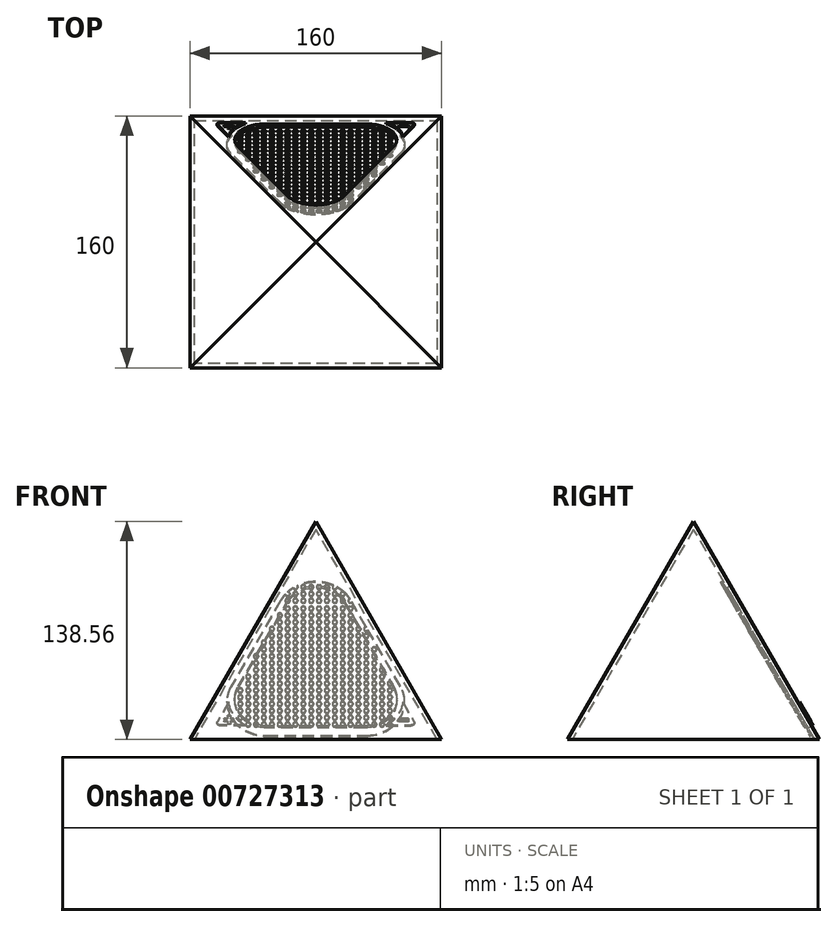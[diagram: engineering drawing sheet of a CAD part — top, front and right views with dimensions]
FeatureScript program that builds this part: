
annotation { "Feature Type Name" : "Feature", "Feature Type Description" : "" }
export const myFeature = defineFeature(function(context is Context, id is Id, definition is map)
    precondition{}
    {
        {
            var Q0;
            Q0=qCreatedBy(makeId("Top.planeOp"),FACE);
            var sketch = newSketch(context, id + "F0", { "sketchPlane" : qUnion([Q0])});
            skLineSegment(sketch, "E0.bottom", {"start": v(-50, 80) * mm, "end": v(50, 80) * mm});
            skLineSegment(sketch, "E0.top", {"start": v(-50, -80) * mm, "end": v(50, -80) * mm});
            skLineSegment(sketch, "E0.left", {"start": v(-80, 50) * mm, "end": v(-80, -50) * mm});
            skLineSegment(sketch, "E0.right", {"start": v(80, 50) * mm, "end": v(80, -50) * mm});
            skPoint(sketch, "E0.middle", {"position": v(0, 0) * mm});
            skLineSegment(sketch, "E1", {"start": v(-50, 80) * mm, "end": v(-50, -80) * mm, "construction": true});
            skLineSegment(sketch, "E2", {"start": v(50, 80) * mm, "end": v(50, -80) * mm, "construction": true});
            skLineSegment(sketch, "E3", {"start": v(80, 50) * mm, "end": v(-80, 50) * mm, "construction": true});
            skLineSegment(sketch, "E4", {"start": v(80, -50) * mm, "end": v(-80, -50) * mm, "construction": true});
            skPoint(sketch, "E5.orphan", {"position": v(-80, 80) * mm});
            skPoint(sketch, "E6.orphan", {"position": v(80, 80) * mm});
            skPoint(sketch, "E7.orphan", {"position": v(80, -80) * mm});
            skPoint(sketch, "E8.orphan", {"position": v(-80, -80) * mm});
            skLineSegment(sketch, "E9", {"start": v(-50, 80) * mm, "end": v(-80, 80) * mm});
            skLineSegment(sketch, "E10", {"start": v(-80, 80) * mm, "end": v(-80, 50) * mm});
            skLineSegment(sketch, "E11", {"start": v(80, 50) * mm, "end": v(80, 80) * mm});
            skLineSegment(sketch, "E12", {"start": v(80, 80) * mm, "end": v(50, 80) * mm});
            skLineSegment(sketch, "E13", {"start": v(80, -50) * mm, "end": v(80, -80) * mm});
            skLineSegment(sketch, "E14", {"start": v(80, -80) * mm, "end": v(50, -80) * mm});
            skLineSegment(sketch, "E15", {"start": v(-50, -80) * mm, "end": v(-80, -80) * mm});
            skLineSegment(sketch, "E16", {"start": v(-80, -80) * mm, "end": v(-80, -50) * mm});
            skSolve(sketch);
        }
        {
            var Q0;
            Q0=makeQuery(id+"F0.imprint","IMPRINT",FACE,{"disambiguationData":[TD([[makeQuery(id+"F0.imprint","IMPRINT",EDGE,{"derivedFrom":sQuery(id+"F0.wireOp",EDGE,"E0.bottom")}),-1.0]])]});
            extrude(context, id + "F1", {"entities" : qUnion([Q0]), "depth" : 139 * mm, "hasDraft" : true, "draftAngle" : 30 * degree, "draftPullDirection" : true});
        }
        {
            var Q0;
            Q0=makeQuery(id+"F1.opExtrude","CAP_FACE",FACE,{"disambiguationData":[OSD([sQuery(id+"F0.wireOp",EDGE,"E0.bottom"),sQuery(id+"F0.wireOp",EDGE,"E0.top"),sQuery(id+"F0.wireOp",EDGE,"E0.left"),sQuery(id+"F0.wireOp",EDGE,"E0.right"),sQuery(id+"F0.wireOp",EDGE,"E9"),sQuery(id+"F0.wireOp",EDGE,"E10"),sQuery(id+"F0.wireOp",EDGE,"E11"),sQuery(id+"F0.wireOp",EDGE,"E12"),sQuery(id+"F0.wireOp",EDGE,"E13"),sQuery(id+"F0.wireOp",EDGE,"E14"),sQuery(id+"F0.wireOp",EDGE,"E15"),sQuery(id+"F0.wireOp",EDGE,"E16")])],"isStart":true});
            shell(context, id + "F2", {"entities" : qUnion([Q0]), "thickness" : 2.5 * mm});
        }
        {
            var Q0;
            Q0=makeQuery(id+"F1.opExtrude","SWEPT_FACE",FACE,{"disambiguationData":[OSD([sQuery(id+"F0.wireOp",EDGE,"E0.bottom"),sQuery(id+"F0.wireOp",EDGE,"E9"),sQuery(id+"F0.wireOp",EDGE,"E12")])]});
            var sketch = newSketch(context, id + "F3", { "sketchPlane" : qUnion([Q0])});
            skCircle(sketch, "E17", {"center": v(0, 20) * mm, "radius": 33 * mm});
            skSolve(sketch);
        }
        {
            var Q0;
            Q0=makeQuery(id+"F3.imprint","IMPRINT",FACE,{"disambiguationData":[TD([[makeQuery(id+"F3.imprint","IMPRINT",EDGE,{"derivedFrom":sQuery(id+"F3.wireOp",EDGE,"E17")}),-1.0]])]});
            var sketch = newSketch(context, id + "F4", { "sketchPlane" : qUnion([Q0])});
            skCircle(sketch, "E18.0", {"center": v(0, 20) * mm, "radius": 33 * mm, "construction": true});
            skLineSegment(sketch, "E19.0", {"start": v(-31.46, -30) * mm, "end": v(31.46, -30) * mm});
            skLineSegment(sketch, "E19.1", {"start": v(-17.89, 61.86) * mm, "end": v(-49.35, -1.06) * mm});
            skLineSegment(sketch, "E19.2", {"start": v(49.35, -1.06) * mm, "end": v(17.89, 61.86) * mm});
            skPoint(sketch, "E20.visualSharp", {"position": v(0, 97.64) * mm});
            skArc(sketch, "E20.filletArc", {"start": v(17.89, 61.86) * mm, "mid": v(0, 72.92) * mm, "end": v(-17.89, 61.86) * mm});
            skPoint(sketch, "E21.visualSharp", {"position": v(63.82, -30) * mm});
            skArc(sketch, "E21.filletArc", {"start": v(31.46, -30) * mm, "mid": v(48.47, -20.51) * mm, "end": v(49.35, -1.06) * mm});
            skPoint(sketch, "E22.visualSharp", {"position": v(-63.82, -30) * mm});
            skArc(sketch, "E22.filletArc", {"start": v(-49.35, -1.06) * mm, "mid": v(-48.47, -20.51) * mm, "end": v(-31.46, -30) * mm});
            skSolve(sketch);
        }
        {
            var Q0;
            Q0=qSketchRegion(id+"F4",true);
            extrude(context, id + "F5", {"entities" : qUnion([Q0]), "operationType" : NewBodyOperationType.REMOVE, "oppositeDirection" : true, "depth" : 25 * mm, "offsetDistance" : 25 * mm});
        }
        {
            var Q0;
            Q0=makeQuery(id+"F3.imprint","IMPRINT",FACE,{"disambiguationData":[TD([[makeQuery(id+"F3.imprint","IMPRINT",EDGE,{"derivedFrom":sQuery(id+"F3.wireOp",EDGE,"E17")}),-1.0]])]});
            var sketch = newSketch(context, id + "F6", { "sketchPlane" : qUnion([Q0])});
            skArc(sketch, "E23.2", {"start": v(-55.28, -12.92) * mm, "mid": v(-51.87, -22.62) * mm, "end": v(-44.73, -30) * mm});
            skLineSegment(sketch, "E24", {"start": v(-44.73, -30) * mm, "end": v(-60.58, -30) * mm});
            skPoint(sketch, "E24.startSnap0", {"position": v(0, -34) * mm});
            skPoint(sketch, "E25.visualSharp", {"position": v(-63.82, -30) * mm});
            skArc(sketch, "E25.filletArc", {"start": v(-62.37, -27.1) * mm, "mid": v(-62.28, -29.05) * mm, "end": v(-60.58, -30) * mm});
            skPoint(sketch, "E26.orphan", {"position": v(-31.46, -34) * mm});
            skPoint(sketch, "E27.orphan", {"position": v(0, -30) * mm});
            skLineSegment(sketch, "E28.trimOffspring", {"start": v(-55.28, -12.92) * mm, "end": v(-62.37, -27.1) * mm});
            skPoint(sketch, "E29.0.start.orphan", {"position": v(-17.89, 61.86) * mm});
            skPoint(sketch, "E30.end.orphan", {"position": v(-49.35, -1.06) * mm});
            skPoint(sketch, "E23.0.start.orphan", {"position": v(31.46, -34) * mm});
            skPoint(sketch, "E31.0", {"position": v(0, 0) * mm});
            skLineSegment(sketch, "E32", {"start": v(0, 0) * mm, "end": v(0, 39.55) * mm, "construction": true});
            skLineSegment(sketch, "E33.MirrorCS", {"start": v(55.28, -12.92) * mm, "end": v(62.37, -27.1) * mm});
            skArc(sketch, "E34.MirrorCS", {"start": v(55.28, -12.92) * mm, "mid": v(51.87, -22.62) * mm, "end": v(44.73, -30) * mm});
            skLineSegment(sketch, "E35.MirrorCS", {"start": v(44.73, -30) * mm, "end": v(60.58, -30) * mm});
            skArc(sketch, "E36.MirrorCS", {"start": v(62.37, -27.1) * mm, "mid": v(62.28, -29.05) * mm, "end": v(60.58, -30) * mm});
            skSolve(sketch);
        }
        {
            var Q0;
            Q0=makeQuery(id+"F6.imprint","IMPRINT",FACE,{"disambiguationData":[TD([[makeQuery(id+"F6.imprint","IMPRINT",EDGE,{"derivedFrom":sQuery(id+"F6.wireOp",EDGE,"E23.2")}),-1.0]])]});
            var Q1;
            Q1=makeQuery(id+"F6.imprint","IMPRINT",FACE,{"disambiguationData":[TD([[makeQuery(id+"F6.imprint","IMPRINT",EDGE,{"derivedFrom":sQuery(id+"F6.wireOp",EDGE,"E33.MirrorCS")}),-1.0]])]});
            extrude(context, id + "F7", {"entities" : qUnion([Q0, Q1]), "operationType" : NewBodyOperationType.ADD, "depth" : 1 * mm, "offsetDistance" : 25 * mm});
        }
        {
            var Q0;
            Q0=makeQuery(id+"F7.opExtrude","CAP_FACE",FACE,{"disambiguationData":[OSD([sQuery(id+"F6.wireOp",EDGE,"E23.2"),sQuery(id+"F6.wireOp",EDGE,"E24"),sQuery(id+"F6.wireOp",EDGE,"E25.filletArc"),sQuery(id+"F6.wireOp",EDGE,"E28.trimOffspring")])],"isStart":false});
            var sketch = newSketch(context, id + "F8", { "sketchPlane" : qUnion([Q0])});
            skLineSegment(sketch, "E37.bottom", {"start": v(-58.9, -25) * mm, "end": v(-52.9, -25) * mm});
            skLineSegment(sketch, "E37.top", {"start": v(-58.9, -27) * mm, "end": v(-52.9, -27) * mm});
            skLineSegment(sketch, "E37.left", {"start": v(-58.9, -25) * mm, "end": v(-58.9, -27) * mm});
            skLineSegment(sketch, "E37.right", {"start": v(-52.9, -25) * mm, "end": v(-52.9, -27) * mm});
            skLineSegment(sketch, "E38.bottom", {"start": v(52.13, -25) * mm, "end": v(54.13, -25) * mm});
            skLineSegment(sketch, "E38.top", {"start": v(52.13, -27) * mm, "end": v(54.13, -27) * mm});
            skLineSegment(sketch, "E38.left", {"start": v(52.13, -25) * mm, "end": v(52.13, -27) * mm});
            skLineSegment(sketch, "E38.right", {"start": v(58.13, -25) * mm, "end": v(58.13, -27) * mm});
            skLineSegment(sketch, "E39.bottom", {"start": v(54.13, -23) * mm, "end": v(56.13, -23) * mm});
            skLineSegment(sketch, "E39.top", {"start": v(54.13, -29) * mm, "end": v(56.13, -29) * mm});
            skLineSegment(sketch, "E39.left", {"start": v(54.13, -23) * mm, "end": v(54.13, -25) * mm});
            skLineSegment(sketch, "E39.right", {"start": v(56.13, -23) * mm, "end": v(56.13, -25) * mm});
            skPoint(sketch, "E39.middle", {"position": v(55.13, -26) * mm});
            skPoint(sketch, "E39.middle.positionSnap0", {"position": v(55.13, -27) * mm});
            skPoint(sketch, "E39.centerSnap0", {"position": v(55.13, -27) * mm});
            skLineSegment(sketch, "E40.trimOffspring", {"start": v(54.13, -27) * mm, "end": v(54.13, -29) * mm});
            skLineSegment(sketch, "E41.trimOffspring", {"start": v(56.13, -25) * mm, "end": v(58.13, -25) * mm});
            skLineSegment(sketch, "E42.trimOffspring", {"start": v(56.13, -27) * mm, "end": v(56.13, -29) * mm});
            skLineSegment(sketch, "E43.trimOffspring", {"start": v(56.13, -27) * mm, "end": v(58.13, -27) * mm});
            skSolve(sketch);
        }
        {
            var Q0;
            Q0=makeQuery(id+"F8.imprint","IMPRINT",FACE,{"disambiguationData":[TD([[makeQuery(id+"F8.imprint","IMPRINT",EDGE,{"derivedFrom":sQuery(id+"F8.wireOp",EDGE,"E37.bottom")}),-1.0]])]});
            var Q1;
            Q1=makeQuery(id+"F8.imprint","IMPRINT",FACE,{"disambiguationData":[TD([[makeQuery(id+"F8.imprint","IMPRINT",EDGE,{"derivedFrom":sQuery(id+"F8.wireOp",EDGE,"E38.bottom")}),-1.0]])]});
            extrude(context, id + "F9", {"entities" : qUnion([Q0, Q1]), "operationType" : NewBodyOperationType.REMOVE, "oppositeDirection" : true, "depth" : 1 * mm, "offsetDistance" : 25 * mm});
        }
        {
            var Q0;
            Q0=qCreatedBy(makeId("Right.planeOp"),FACE);
            var sketch = newSketch(context, id + "F10", { "sketchPlane" : qUnion([Q0])});
            skPoint(sketch, "E44.0", {"position": v(73.92, 8.04) * mm});
            skCircle(sketch, "E45", {"center": v(73.92, 8.04) * mm, "radius": 1.5 * mm});
            skSolve(sketch);
        }
        {
            var Q0;
            Q0=makeQuery(id+"F2.opShell","OFFSET_FACE",FACE,{"disambiguationData":[OSD([sQuery(id+"F0.wireOp",EDGE,"E0.bottom"),sQuery(id+"F0.wireOp",EDGE,"E9"),sQuery(id+"F0.wireOp",EDGE,"E12")])]});
            cPlane(context, id + "F11", {"entities" : qUnion([Q0]), "cplaneType" : CPlaneType.OFFSET, "offset" : 1 * mm, "width" : 150 * mm, "height" : 150 * mm});
        }
        {
            var Q0;
            Q0=qCreatedBy(id+"F11.planeOp",FACE);
            var sketch = newSketch(context, id + "F12", { "sketchPlane" : qUnion([Q0])});
            skArc(sketch, "E46.0", {"start": v(22.36, 64.1) * mm, "mid": v(0, 77.92) * mm, "end": v(-22.36, 64.1) * mm});
            skArc(sketch, "E46.1", {"start": v(-53.82, 1.18) * mm, "mid": v(-52.73, -23.14) * mm, "end": v(-31.46, -35) * mm});
            skLineSegment(sketch, "E46.2", {"start": v(-31.46, -35) * mm, "end": v(31.46, -35) * mm});
            skLineSegment(sketch, "E46.3", {"start": v(-22.36, 64.1) * mm, "end": v(-53.82, 1.18) * mm});
            skArc(sketch, "E46.4", {"start": v(31.46, -35) * mm, "mid": v(52.73, -23.14) * mm, "end": v(53.82, 1.18) * mm});
            skLineSegment(sketch, "E46.5", {"start": v(53.82, 1.18) * mm, "end": v(22.36, 64.1) * mm});
            skSolve(sketch);
        }
        {
            var Q0;
            Q0=qSketchRegion(id+"F12",true);
            extrude(context, id + "F13", {"entities" : qUnion([Q0]), "depth" : 1 * mm, "offsetDistance" : 25 * mm});
        }
        {
            var Q0;
            Q0=makeQuery(id+"F13.opExtrude","CAP_FACE",FACE,{"disambiguationData":[OSD([sQuery(id+"F12.wireOp",EDGE,"E46.0"),sQuery(id+"F12.wireOp",EDGE,"E46.1"),sQuery(id+"F12.wireOp",EDGE,"E46.2"),sQuery(id+"F12.wireOp",EDGE,"E46.3"),sQuery(id+"F12.wireOp",EDGE,"E46.4"),sQuery(id+"F12.wireOp",EDGE,"E46.5")])],"isStart":false});
            var sketch = newSketch(context, id + "F14", { "sketchPlane" : qUnion([Q0])});
            skCircle(sketch, "E47.0.1.2", {"center": v(-22.93, -26.66) * mm, "radius": 1.5 * mm});
            skCircle(sketch, "E47.0.1.4", {"center": v(-7.93, -26.66) * mm, "radius": 1.5 * mm});
            skCircle(sketch, "E47.0.1.5", {"center": v(-12.93, -26.66) * mm, "radius": 1.5 * mm});
            skCircle(sketch, "E47.0.1.6", {"center": v(-37.93, -26.66) * mm, "radius": 1.5 * mm});
            skCircle(sketch, "E47.0.1.9", {"center": v(42.07, -26.66) * mm, "radius": 1.5 * mm});
            skCircle(sketch, "E47.0.1.10", {"center": v(27.07, -26.66) * mm, "radius": 1.5 * mm});
            skCircle(sketch, "E47.0.1.11", {"center": v(17.07, -26.66) * mm, "radius": 1.5 * mm});
            skCircle(sketch, "E47.0.1.12", {"center": v(2.07, -26.66) * mm, "radius": 1.5 * mm});
            skCircle(sketch, "E47.0.1.14", {"center": v(-32.93, -26.66) * mm, "radius": 1.5 * mm});
            skCircle(sketch, "E47.0.1.15", {"center": v(-17.93, -26.66) * mm, "radius": 1.5 * mm});
            skCircle(sketch, "E47.0.1.16", {"center": v(-27.93, -26.66) * mm, "radius": 1.5 * mm});
            skCircle(sketch, "E47.0.1.17", {"center": v(47.07, -26.66) * mm, "radius": 1.5 * mm});
            skCircle(sketch, "E47.0.1.18", {"center": v(37.07, -26.66) * mm, "radius": 1.5 * mm});
            skCircle(sketch, "E47.0.1.19", {"center": v(32.07, -26.66) * mm, "radius": 1.5 * mm});
            skCircle(sketch, "E47.0.1.20", {"center": v(22.07, -26.66) * mm, "radius": 1.5 * mm});
            skCircle(sketch, "E47.0.1.21", {"center": v(12.07, -26.66) * mm, "radius": 1.5 * mm});
            skCircle(sketch, "E47.0.1.22", {"center": v(7.07, -26.66) * mm, "radius": 1.5 * mm});
            skCircle(sketch, "E47.0.1.23", {"center": v(-2.93, -26.66) * mm, "radius": 1.5 * mm});
            skCircle(sketch, "E47.0.1.25", {"center": v(-42.93, -26.66) * mm, "radius": 1.5 * mm});
            skCircle(sketch, "E47.0.2.2", {"center": v(-22.93, -21.66) * mm, "radius": 1.5 * mm});
            skCircle(sketch, "E47.0.2.3", {"center": v(-47.93, -21.66) * mm, "radius": 1.5 * mm});
            skCircle(sketch, "E47.0.2.4", {"center": v(-7.93, -21.66) * mm, "radius": 1.5 * mm});
            skCircle(sketch, "E47.0.2.5", {"center": v(-12.93, -21.66) * mm, "radius": 1.5 * mm});
            skCircle(sketch, "E47.0.2.6", {"center": v(-37.93, -21.66) * mm, "radius": 1.5 * mm});
            skCircle(sketch, "E47.0.2.9", {"center": v(42.07, -21.66) * mm, "radius": 1.5 * mm});
            skCircle(sketch, "E47.0.2.10", {"center": v(27.07, -21.66) * mm, "radius": 1.5 * mm});
            skCircle(sketch, "E47.0.2.11", {"center": v(17.07, -21.66) * mm, "radius": 1.5 * mm});
            skCircle(sketch, "E47.0.2.12", {"center": v(2.07, -21.66) * mm, "radius": 1.5 * mm});
            skCircle(sketch, "E47.0.2.14", {"center": v(-32.93, -21.66) * mm, "radius": 1.5 * mm});
            skCircle(sketch, "E47.0.2.15", {"center": v(-17.93, -21.66) * mm, "radius": 1.5 * mm});
            skCircle(sketch, "E47.0.2.16", {"center": v(-27.93, -21.66) * mm, "radius": 1.5 * mm});
            skCircle(sketch, "E47.0.2.17", {"center": v(47.07, -21.66) * mm, "radius": 1.5 * mm});
            skCircle(sketch, "E47.0.2.18", {"center": v(37.07, -21.66) * mm, "radius": 1.5 * mm});
            skCircle(sketch, "E47.0.2.19", {"center": v(32.07, -21.66) * mm, "radius": 1.5 * mm});
            skCircle(sketch, "E47.0.2.20", {"center": v(22.07, -21.66) * mm, "radius": 1.5 * mm});
            skCircle(sketch, "E47.0.2.21", {"center": v(12.07, -21.66) * mm, "radius": 1.5 * mm});
            skCircle(sketch, "E47.0.2.22", {"center": v(7.07, -21.66) * mm, "radius": 1.5 * mm});
            skCircle(sketch, "E47.0.2.23", {"center": v(-2.93, -21.66) * mm, "radius": 1.5 * mm});
            skCircle(sketch, "E47.0.2.25", {"center": v(-42.93, -21.66) * mm, "radius": 1.5 * mm});
            skCircle(sketch, "E47.0.3.2", {"center": v(-22.93, -16.66) * mm, "radius": 1.5 * mm});
            skCircle(sketch, "E47.0.3.3", {"center": v(-47.93, -16.66) * mm, "radius": 1.5 * mm});
            skCircle(sketch, "E47.0.3.4", {"center": v(-7.93, -16.66) * mm, "radius": 1.5 * mm});
            skCircle(sketch, "E47.0.3.5", {"center": v(-12.93, -16.66) * mm, "radius": 1.5 * mm});
            skCircle(sketch, "E47.0.3.6", {"center": v(-37.93, -16.66) * mm, "radius": 1.5 * mm});
            skCircle(sketch, "E47.0.3.9", {"center": v(42.07, -16.66) * mm, "radius": 1.5 * mm});
            skCircle(sketch, "E47.0.3.10", {"center": v(27.07, -16.66) * mm, "radius": 1.5 * mm});
            skCircle(sketch, "E47.0.3.11", {"center": v(17.07, -16.66) * mm, "radius": 1.5 * mm});
            skCircle(sketch, "E47.0.3.12", {"center": v(2.07, -16.66) * mm, "radius": 1.5 * mm});
            skCircle(sketch, "E47.0.3.14", {"center": v(-32.93, -16.66) * mm, "radius": 1.5 * mm});
            skCircle(sketch, "E47.0.3.15", {"center": v(-17.93, -16.66) * mm, "radius": 1.5 * mm});
            skCircle(sketch, "E47.0.3.16", {"center": v(-27.93, -16.66) * mm, "radius": 1.5 * mm});
            skCircle(sketch, "E47.0.3.17", {"center": v(47.07, -16.66) * mm, "radius": 1.5 * mm});
            skCircle(sketch, "E47.0.3.18", {"center": v(37.07, -16.66) * mm, "radius": 1.5 * mm});
            skCircle(sketch, "E47.0.3.19", {"center": v(32.07, -16.66) * mm, "radius": 1.5 * mm});
            skCircle(sketch, "E47.0.3.20", {"center": v(22.07, -16.66) * mm, "radius": 1.5 * mm});
            skCircle(sketch, "E47.0.3.21", {"center": v(12.07, -16.66) * mm, "radius": 1.5 * mm});
            skCircle(sketch, "E47.0.3.22", {"center": v(7.07, -16.66) * mm, "radius": 1.5 * mm});
            skCircle(sketch, "E47.0.3.23", {"center": v(-2.93, -16.66) * mm, "radius": 1.5 * mm});
            skCircle(sketch, "E47.0.3.25", {"center": v(-42.93, -16.66) * mm, "radius": 1.5 * mm});
            skCircle(sketch, "E47.0.4.2", {"center": v(-22.93, -11.66) * mm, "radius": 1.5 * mm});
            skCircle(sketch, "E47.0.4.3", {"center": v(-47.93, -11.66) * mm, "radius": 1.5 * mm});
            skCircle(sketch, "E47.0.4.4", {"center": v(-7.93, -11.66) * mm, "radius": 1.5 * mm});
            skCircle(sketch, "E47.0.4.5", {"center": v(-12.93, -11.66) * mm, "radius": 1.5 * mm});
            skCircle(sketch, "E47.0.4.6", {"center": v(-37.93, -11.66) * mm, "radius": 1.5 * mm});
            skCircle(sketch, "E47.0.4.9", {"center": v(42.07, -11.66) * mm, "radius": 1.5 * mm});
            skCircle(sketch, "E47.0.4.10", {"center": v(27.07, -11.66) * mm, "radius": 1.5 * mm});
            skCircle(sketch, "E47.0.4.11", {"center": v(17.07, -11.66) * mm, "radius": 1.5 * mm});
            skCircle(sketch, "E47.0.4.12", {"center": v(2.07, -11.66) * mm, "radius": 1.5 * mm});
            skCircle(sketch, "E47.0.4.14", {"center": v(-32.93, -11.66) * mm, "radius": 1.5 * mm});
            skCircle(sketch, "E47.0.4.15", {"center": v(-17.93, -11.66) * mm, "radius": 1.5 * mm});
            skCircle(sketch, "E47.0.4.16", {"center": v(-27.93, -11.66) * mm, "radius": 1.5 * mm});
            skCircle(sketch, "E47.0.4.17", {"center": v(47.07, -11.66) * mm, "radius": 1.5 * mm});
            skCircle(sketch, "E47.0.4.18", {"center": v(37.07, -11.66) * mm, "radius": 1.5 * mm});
            skCircle(sketch, "E47.0.4.19", {"center": v(32.07, -11.66) * mm, "radius": 1.5 * mm});
            skCircle(sketch, "E47.0.4.20", {"center": v(22.07, -11.66) * mm, "radius": 1.5 * mm});
            skCircle(sketch, "E47.0.4.21", {"center": v(12.07, -11.66) * mm, "radius": 1.5 * mm});
            skCircle(sketch, "E47.0.4.22", {"center": v(7.07, -11.66) * mm, "radius": 1.5 * mm});
            skCircle(sketch, "E47.0.4.23", {"center": v(-2.93, -11.66) * mm, "radius": 1.5 * mm});
            skCircle(sketch, "E47.0.4.25", {"center": v(-42.93, -11.66) * mm, "radius": 1.5 * mm});
            skCircle(sketch, "E47.0.5.2", {"center": v(-22.93, -6.66) * mm, "radius": 1.5 * mm});
            skCircle(sketch, "E47.0.5.3", {"center": v(-47.93, -6.66) * mm, "radius": 1.5 * mm});
            skCircle(sketch, "E47.0.5.4", {"center": v(-7.93, -6.66) * mm, "radius": 1.5 * mm});
            skCircle(sketch, "E47.0.5.5", {"center": v(-12.93, -6.66) * mm, "radius": 1.5 * mm});
            skCircle(sketch, "E47.0.5.6", {"center": v(-37.93, -6.66) * mm, "radius": 1.5 * mm});
            skCircle(sketch, "E47.0.5.9", {"center": v(42.07, -6.66) * mm, "radius": 1.5 * mm});
            skCircle(sketch, "E47.0.5.10", {"center": v(27.07, -6.66) * mm, "radius": 1.5 * mm});
            skCircle(sketch, "E47.0.5.11", {"center": v(17.07, -6.66) * mm, "radius": 1.5 * mm});
            skCircle(sketch, "E47.0.5.12", {"center": v(2.07, -6.66) * mm, "radius": 1.5 * mm});
            skCircle(sketch, "E47.0.5.14", {"center": v(-32.93, -6.66) * mm, "radius": 1.5 * mm});
            skCircle(sketch, "E47.0.5.15", {"center": v(-17.93, -6.66) * mm, "radius": 1.5 * mm});
            skCircle(sketch, "E47.0.5.16", {"center": v(-27.93, -6.66) * mm, "radius": 1.5 * mm});
            skCircle(sketch, "E47.0.5.17", {"center": v(47.07, -6.66) * mm, "radius": 1.5 * mm});
            skCircle(sketch, "E47.0.5.18", {"center": v(37.07, -6.66) * mm, "radius": 1.5 * mm});
            skCircle(sketch, "E47.0.5.19", {"center": v(32.07, -6.66) * mm, "radius": 1.5 * mm});
            skCircle(sketch, "E47.0.5.20", {"center": v(22.07, -6.66) * mm, "radius": 1.5 * mm});
            skCircle(sketch, "E47.0.5.21", {"center": v(12.07, -6.66) * mm, "radius": 1.5 * mm});
            skCircle(sketch, "E47.0.5.22", {"center": v(7.07, -6.66) * mm, "radius": 1.5 * mm});
            skCircle(sketch, "E47.0.5.23", {"center": v(-2.93, -6.66) * mm, "radius": 1.5 * mm});
            skCircle(sketch, "E47.0.5.25", {"center": v(-42.93, -6.66) * mm, "radius": 1.5 * mm});
            skCircle(sketch, "E47.0.6.2", {"center": v(-22.93, -1.66) * mm, "radius": 1.5 * mm});
            skCircle(sketch, "E47.0.6.3", {"center": v(-47.93, -1.66) * mm, "radius": 1.5 * mm});
            skCircle(sketch, "E47.0.6.4", {"center": v(-7.93, -1.66) * mm, "radius": 1.5 * mm});
            skCircle(sketch, "E47.0.6.5", {"center": v(-12.93, -1.66) * mm, "radius": 1.5 * mm});
            skCircle(sketch, "E47.0.6.6", {"center": v(-37.93, -1.66) * mm, "radius": 1.5 * mm});
            skCircle(sketch, "E47.0.6.9", {"center": v(42.07, -1.66) * mm, "radius": 1.5 * mm});
            skCircle(sketch, "E47.0.6.10", {"center": v(27.07, -1.66) * mm, "radius": 1.5 * mm});
            skCircle(sketch, "E47.0.6.11", {"center": v(17.07, -1.66) * mm, "radius": 1.5 * mm});
            skCircle(sketch, "E47.0.6.12", {"center": v(2.07, -1.66) * mm, "radius": 1.5 * mm});
            skCircle(sketch, "E47.0.6.14", {"center": v(-32.93, -1.66) * mm, "radius": 1.5 * mm});
            skCircle(sketch, "E47.0.6.15", {"center": v(-17.93, -1.66) * mm, "radius": 1.5 * mm});
            skCircle(sketch, "E47.0.6.16", {"center": v(-27.93, -1.66) * mm, "radius": 1.5 * mm});
            skCircle(sketch, "E47.0.6.17", {"center": v(47.07, -1.66) * mm, "radius": 1.5 * mm});
            skCircle(sketch, "E47.0.6.18", {"center": v(37.07, -1.66) * mm, "radius": 1.5 * mm});
            skCircle(sketch, "E47.0.6.19", {"center": v(32.07, -1.66) * mm, "radius": 1.5 * mm});
            skCircle(sketch, "E47.0.6.20", {"center": v(22.07, -1.66) * mm, "radius": 1.5 * mm});
            skCircle(sketch, "E47.0.6.21", {"center": v(12.07, -1.66) * mm, "radius": 1.5 * mm});
            skCircle(sketch, "E47.0.6.22", {"center": v(7.07, -1.66) * mm, "radius": 1.5 * mm});
            skCircle(sketch, "E47.0.6.23", {"center": v(-2.93, -1.66) * mm, "radius": 1.5 * mm});
            skCircle(sketch, "E47.0.6.25", {"center": v(-42.93, -1.66) * mm, "radius": 1.5 * mm});
            skCircle(sketch, "E47.0.7.2", {"center": v(-22.93, 3.34) * mm, "radius": 1.5 * mm});
            skCircle(sketch, "E47.0.7.4", {"center": v(-7.93, 3.34) * mm, "radius": 1.5 * mm});
            skCircle(sketch, "E47.0.7.5", {"center": v(-12.93, 3.34) * mm, "radius": 1.5 * mm});
            skCircle(sketch, "E47.0.7.6", {"center": v(-37.93, 3.34) * mm, "radius": 1.5 * mm});
            skCircle(sketch, "E47.0.7.9", {"center": v(42.07, 3.34) * mm, "radius": 1.5 * mm});
            skCircle(sketch, "E47.0.7.10", {"center": v(27.07, 3.34) * mm, "radius": 1.5 * mm});
            skCircle(sketch, "E47.0.7.11", {"center": v(17.07, 3.34) * mm, "radius": 1.5 * mm});
            skCircle(sketch, "E47.0.7.12", {"center": v(2.07, 3.34) * mm, "radius": 1.5 * mm});
            skCircle(sketch, "E47.0.7.14", {"center": v(-32.93, 3.34) * mm, "radius": 1.5 * mm});
            skCircle(sketch, "E47.0.7.15", {"center": v(-17.93, 3.34) * mm, "radius": 1.5 * mm});
            skCircle(sketch, "E47.0.7.16", {"center": v(-27.93, 3.34) * mm, "radius": 1.5 * mm});
            skCircle(sketch, "E47.0.7.17", {"center": v(47.07, 3.34) * mm, "radius": 1.5 * mm});
            skCircle(sketch, "E47.0.7.18", {"center": v(37.07, 3.34) * mm, "radius": 1.5 * mm});
            skCircle(sketch, "E47.0.7.19", {"center": v(32.07, 3.34) * mm, "radius": 1.5 * mm});
            skCircle(sketch, "E47.0.7.20", {"center": v(22.07, 3.34) * mm, "radius": 1.5 * mm});
            skCircle(sketch, "E47.0.7.21", {"center": v(12.07, 3.34) * mm, "radius": 1.5 * mm});
            skCircle(sketch, "E47.0.7.22", {"center": v(7.07, 3.34) * mm, "radius": 1.5 * mm});
            skCircle(sketch, "E47.0.7.23", {"center": v(-2.93, 3.34) * mm, "radius": 1.5 * mm});
            skCircle(sketch, "E47.0.7.25", {"center": v(-42.93, 3.34) * mm, "radius": 1.5 * mm});
            skLineSegment(sketch, "E47.0.8.0", {"start": v(57.07, 8.34) * mm, "end": v(52.07, 8.34) * mm, "construction": true});
            skCircle(sketch, "E47.0.8.2", {"center": v(-22.93, 8.34) * mm, "radius": 1.5 * mm});
            skCircle(sketch, "E47.0.8.4", {"center": v(-7.93, 8.34) * mm, "radius": 1.5 * mm});
            skCircle(sketch, "E47.0.8.5", {"center": v(-12.93, 8.34) * mm, "radius": 1.5 * mm});
            skCircle(sketch, "E47.0.8.6", {"center": v(-37.93, 8.34) * mm, "radius": 1.5 * mm});
            skCircle(sketch, "E47.0.8.9", {"center": v(42.07, 8.34) * mm, "radius": 1.5 * mm});
            skCircle(sketch, "E47.0.8.10", {"center": v(27.07, 8.34) * mm, "radius": 1.5 * mm});
            skCircle(sketch, "E47.0.8.11", {"center": v(17.07, 8.34) * mm, "radius": 1.5 * mm});
            skCircle(sketch, "E47.0.8.12", {"center": v(2.07, 8.34) * mm, "radius": 1.5 * mm});
            skCircle(sketch, "E47.0.8.14", {"center": v(-32.93, 8.34) * mm, "radius": 1.5 * mm});
            skCircle(sketch, "E47.0.8.15", {"center": v(-17.93, 8.34) * mm, "radius": 1.5 * mm});
            skCircle(sketch, "E47.0.8.16", {"center": v(-27.93, 8.34) * mm, "radius": 1.5 * mm});
            skCircle(sketch, "E47.0.8.18", {"center": v(37.07, 8.34) * mm, "radius": 1.5 * mm});
            skCircle(sketch, "E47.0.8.19", {"center": v(32.07, 8.34) * mm, "radius": 1.5 * mm});
            skCircle(sketch, "E47.0.8.20", {"center": v(22.07, 8.34) * mm, "radius": 1.5 * mm});
            skCircle(sketch, "E47.0.8.21", {"center": v(12.07, 8.34) * mm, "radius": 1.5 * mm});
            skCircle(sketch, "E47.0.8.22", {"center": v(7.07, 8.34) * mm, "radius": 1.5 * mm});
            skCircle(sketch, "E47.0.8.23", {"center": v(-2.93, 8.34) * mm, "radius": 1.5 * mm});
            skCircle(sketch, "E47.0.8.25", {"center": v(-42.93, 8.34) * mm, "radius": 1.5 * mm});
            skLineSegment(sketch, "E47.0.9.0", {"start": v(57.07, 13.34) * mm, "end": v(52.07, 13.34) * mm, "construction": true});
            skCircle(sketch, "E47.0.9.2", {"center": v(-22.93, 13.34) * mm, "radius": 1.5 * mm});
            skCircle(sketch, "E47.0.9.4", {"center": v(-7.93, 13.34) * mm, "radius": 1.5 * mm});
            skCircle(sketch, "E47.0.9.5", {"center": v(-12.93, 13.34) * mm, "radius": 1.5 * mm});
            skCircle(sketch, "E47.0.9.6", {"center": v(-37.93, 13.34) * mm, "radius": 1.5 * mm});
            skCircle(sketch, "E47.0.9.9", {"center": v(42.07, 13.34) * mm, "radius": 1.5 * mm});
            skCircle(sketch, "E47.0.9.10", {"center": v(27.07, 13.34) * mm, "radius": 1.5 * mm});
            skCircle(sketch, "E47.0.9.11", {"center": v(17.07, 13.34) * mm, "radius": 1.5 * mm});
            skCircle(sketch, "E47.0.9.12", {"center": v(2.07, 13.34) * mm, "radius": 1.5 * mm});
            skCircle(sketch, "E47.0.9.14", {"center": v(-32.93, 13.34) * mm, "radius": 1.5 * mm});
            skCircle(sketch, "E47.0.9.15", {"center": v(-17.93, 13.34) * mm, "radius": 1.5 * mm});
            skCircle(sketch, "E47.0.9.16", {"center": v(-27.93, 13.34) * mm, "radius": 1.5 * mm});
            skCircle(sketch, "E47.0.9.18", {"center": v(37.07, 13.34) * mm, "radius": 1.5 * mm});
            skCircle(sketch, "E47.0.9.19", {"center": v(32.07, 13.34) * mm, "radius": 1.5 * mm});
            skCircle(sketch, "E47.0.9.20", {"center": v(22.07, 13.34) * mm, "radius": 1.5 * mm});
            skCircle(sketch, "E47.0.9.21", {"center": v(12.07, 13.34) * mm, "radius": 1.5 * mm});
            skCircle(sketch, "E47.0.9.22", {"center": v(7.07, 13.34) * mm, "radius": 1.5 * mm});
            skCircle(sketch, "E47.0.9.23", {"center": v(-2.93, 13.34) * mm, "radius": 1.5 * mm});
            skLineSegment(sketch, "E47.0.10.0", {"start": v(57.07, 18.34) * mm, "end": v(52.07, 18.34) * mm, "construction": true});
            skCircle(sketch, "E47.0.10.2", {"center": v(-22.93, 18.34) * mm, "radius": 1.5 * mm});
            skCircle(sketch, "E47.0.10.4", {"center": v(-7.93, 18.34) * mm, "radius": 1.5 * mm});
            skCircle(sketch, "E47.0.10.5", {"center": v(-12.93, 18.34) * mm, "radius": 1.5 * mm});
            skCircle(sketch, "E47.0.10.6", {"center": v(-37.93, 18.34) * mm, "radius": 1.5 * mm});
            skCircle(sketch, "E47.0.10.10", {"center": v(27.07, 18.34) * mm, "radius": 1.5 * mm});
            skCircle(sketch, "E47.0.10.11", {"center": v(17.07, 18.34) * mm, "radius": 1.5 * mm});
            skCircle(sketch, "E47.0.10.12", {"center": v(2.07, 18.34) * mm, "radius": 1.5 * mm});
            skCircle(sketch, "E47.0.10.14", {"center": v(-32.93, 18.34) * mm, "radius": 1.5 * mm});
            skCircle(sketch, "E47.0.10.15", {"center": v(-17.93, 18.34) * mm, "radius": 1.5 * mm});
            skCircle(sketch, "E47.0.10.16", {"center": v(-27.93, 18.34) * mm, "radius": 1.5 * mm});
            skCircle(sketch, "E47.0.10.18", {"center": v(37.07, 18.34) * mm, "radius": 1.5 * mm});
            skCircle(sketch, "E47.0.10.19", {"center": v(32.07, 18.34) * mm, "radius": 1.5 * mm});
            skCircle(sketch, "E47.0.10.20", {"center": v(22.07, 18.34) * mm, "radius": 1.5 * mm});
            skCircle(sketch, "E47.0.10.21", {"center": v(12.07, 18.34) * mm, "radius": 1.5 * mm});
            skCircle(sketch, "E47.0.10.22", {"center": v(7.07, 18.34) * mm, "radius": 1.5 * mm});
            skCircle(sketch, "E47.0.10.23", {"center": v(-2.93, 18.34) * mm, "radius": 1.5 * mm});
            skLineSegment(sketch, "E47.0.11.0", {"start": v(57.07, 23.34) * mm, "end": v(52.07, 23.34) * mm, "construction": true});
            skCircle(sketch, "E47.0.11.2", {"center": v(-22.93, 23.34) * mm, "radius": 1.5 * mm});
            skCircle(sketch, "E47.0.11.4", {"center": v(-7.93, 23.34) * mm, "radius": 1.5 * mm});
            skCircle(sketch, "E47.0.11.5", {"center": v(-12.93, 23.34) * mm, "radius": 1.5 * mm});
            skCircle(sketch, "E47.0.11.10", {"center": v(27.07, 23.34) * mm, "radius": 1.5 * mm});
            skCircle(sketch, "E47.0.11.11", {"center": v(17.07, 23.34) * mm, "radius": 1.5 * mm});
            skCircle(sketch, "E47.0.11.12", {"center": v(2.07, 23.34) * mm, "radius": 1.5 * mm});
            skCircle(sketch, "E47.0.11.14", {"center": v(-32.93, 23.34) * mm, "radius": 1.5 * mm});
            skCircle(sketch, "E47.0.11.15", {"center": v(-17.93, 23.34) * mm, "radius": 1.5 * mm});
            skCircle(sketch, "E47.0.11.16", {"center": v(-27.93, 23.34) * mm, "radius": 1.5 * mm});
            skCircle(sketch, "E47.0.11.18", {"center": v(37.07, 23.34) * mm, "radius": 1.5 * mm});
            skCircle(sketch, "E47.0.11.19", {"center": v(32.07, 23.34) * mm, "radius": 1.5 * mm});
            skCircle(sketch, "E47.0.11.20", {"center": v(22.07, 23.34) * mm, "radius": 1.5 * mm});
            skCircle(sketch, "E47.0.11.21", {"center": v(12.07, 23.34) * mm, "radius": 1.5 * mm});
            skCircle(sketch, "E47.0.11.22", {"center": v(7.07, 23.34) * mm, "radius": 1.5 * mm});
            skCircle(sketch, "E47.0.11.23", {"center": v(-2.93, 23.34) * mm, "radius": 1.5 * mm});
            skLineSegment(sketch, "E47.0.12.0", {"start": v(57.07, 28.34) * mm, "end": v(52.07, 28.34) * mm, "construction": true});
            skCircle(sketch, "E47.0.12.2", {"center": v(-22.93, 28.34) * mm, "radius": 1.5 * mm});
            skCircle(sketch, "E47.0.12.4", {"center": v(-7.93, 28.34) * mm, "radius": 1.5 * mm});
            skCircle(sketch, "E47.0.12.5", {"center": v(-12.93, 28.34) * mm, "radius": 1.5 * mm});
            skCircle(sketch, "E47.0.12.10", {"center": v(27.07, 28.34) * mm, "radius": 1.5 * mm});
            skCircle(sketch, "E47.0.12.11", {"center": v(17.07, 28.34) * mm, "radius": 1.5 * mm});
            skCircle(sketch, "E47.0.12.12", {"center": v(2.07, 28.34) * mm, "radius": 1.5 * mm});
            skCircle(sketch, "E47.0.12.14", {"center": v(-32.93, 28.34) * mm, "radius": 1.5 * mm});
            skCircle(sketch, "E47.0.12.15", {"center": v(-17.93, 28.34) * mm, "radius": 1.5 * mm});
            skCircle(sketch, "E47.0.12.16", {"center": v(-27.93, 28.34) * mm, "radius": 1.5 * mm});
            skCircle(sketch, "E47.0.12.18", {"center": v(37.07, 28.34) * mm, "radius": 1.5 * mm});
            skCircle(sketch, "E47.0.12.19", {"center": v(32.07, 28.34) * mm, "radius": 1.5 * mm});
            skCircle(sketch, "E47.0.12.20", {"center": v(22.07, 28.34) * mm, "radius": 1.5 * mm});
            skCircle(sketch, "E47.0.12.21", {"center": v(12.07, 28.34) * mm, "radius": 1.5 * mm});
            skCircle(sketch, "E47.0.12.22", {"center": v(7.07, 28.34) * mm, "radius": 1.5 * mm});
            skCircle(sketch, "E47.0.12.23", {"center": v(-2.93, 28.34) * mm, "radius": 1.5 * mm});
            skLineSegment(sketch, "E47.0.13.0", {"start": v(57.07, 33.34) * mm, "end": v(52.07, 33.34) * mm, "construction": true});
            skCircle(sketch, "E47.0.13.2", {"center": v(-22.93, 33.34) * mm, "radius": 1.5 * mm});
            skCircle(sketch, "E47.0.13.4", {"center": v(-7.93, 33.34) * mm, "radius": 1.5 * mm});
            skCircle(sketch, "E47.0.13.5", {"center": v(-12.93, 33.34) * mm, "radius": 1.5 * mm});
            skCircle(sketch, "E47.0.13.10", {"center": v(27.07, 33.34) * mm, "radius": 1.5 * mm});
            skCircle(sketch, "E47.0.13.11", {"center": v(17.07, 33.34) * mm, "radius": 1.5 * mm});
            skCircle(sketch, "E47.0.13.12", {"center": v(2.07, 33.34) * mm, "radius": 1.5 * mm});
            skCircle(sketch, "E47.0.13.14", {"center": v(-32.93, 33.34) * mm, "radius": 1.5 * mm});
            skCircle(sketch, "E47.0.13.15", {"center": v(-17.93, 33.34) * mm, "radius": 1.5 * mm});
            skCircle(sketch, "E47.0.13.16", {"center": v(-27.93, 33.34) * mm, "radius": 1.5 * mm});
            skCircle(sketch, "E47.0.13.19", {"center": v(32.07, 33.34) * mm, "radius": 1.5 * mm});
            skCircle(sketch, "E47.0.13.20", {"center": v(22.07, 33.34) * mm, "radius": 1.5 * mm});
            skCircle(sketch, "E47.0.13.21", {"center": v(12.07, 33.34) * mm, "radius": 1.5 * mm});
            skCircle(sketch, "E47.0.13.22", {"center": v(7.07, 33.34) * mm, "radius": 1.5 * mm});
            skCircle(sketch, "E47.0.13.23", {"center": v(-2.93, 33.34) * mm, "radius": 1.5 * mm});
            skCircle(sketch, "E47.0.14.2", {"center": v(-22.93, 38.34) * mm, "radius": 1.5 * mm});
            skCircle(sketch, "E47.0.14.4", {"center": v(-7.93, 38.34) * mm, "radius": 1.5 * mm});
            skCircle(sketch, "E47.0.14.5", {"center": v(-12.93, 38.34) * mm, "radius": 1.5 * mm});
            skCircle(sketch, "E47.0.14.10", {"center": v(27.07, 38.34) * mm, "radius": 1.5 * mm});
            skCircle(sketch, "E47.0.14.11", {"center": v(17.07, 38.34) * mm, "radius": 1.5 * mm});
            skCircle(sketch, "E47.0.14.12", {"center": v(2.07, 38.34) * mm, "radius": 1.5 * mm});
            skCircle(sketch, "E47.0.14.15", {"center": v(-17.93, 38.34) * mm, "radius": 1.5 * mm});
            skCircle(sketch, "E47.0.14.16", {"center": v(-27.93, 38.34) * mm, "radius": 1.5 * mm});
            skCircle(sketch, "E47.0.14.19", {"center": v(32.07, 38.34) * mm, "radius": 1.5 * mm});
            skCircle(sketch, "E47.0.14.20", {"center": v(22.07, 38.34) * mm, "radius": 1.5 * mm});
            skCircle(sketch, "E47.0.14.21", {"center": v(12.07, 38.34) * mm, "radius": 1.5 * mm});
            skCircle(sketch, "E47.0.14.22", {"center": v(7.07, 38.34) * mm, "radius": 1.5 * mm});
            skCircle(sketch, "E47.0.14.23", {"center": v(-2.93, 38.34) * mm, "radius": 1.5 * mm});
            skCircle(sketch, "E47.0.15.2", {"center": v(-22.93, 43.34) * mm, "radius": 1.5 * mm});
            skCircle(sketch, "E47.0.15.4", {"center": v(-7.93, 43.34) * mm, "radius": 1.5 * mm});
            skCircle(sketch, "E47.0.15.5", {"center": v(-12.93, 43.34) * mm, "radius": 1.5 * mm});
            skCircle(sketch, "E47.0.15.10", {"center": v(27.07, 43.34) * mm, "radius": 1.5 * mm});
            skCircle(sketch, "E47.0.15.11", {"center": v(17.07, 43.34) * mm, "radius": 1.5 * mm});
            skCircle(sketch, "E47.0.15.12", {"center": v(2.07, 43.34) * mm, "radius": 1.5 * mm});
            skCircle(sketch, "E47.0.15.15", {"center": v(-17.93, 43.34) * mm, "radius": 1.5 * mm});
            skCircle(sketch, "E47.0.15.16", {"center": v(-27.93, 43.34) * mm, "radius": 1.5 * mm});
            skCircle(sketch, "E47.0.15.19", {"center": v(32.07, 43.34) * mm, "radius": 1.5 * mm});
            skCircle(sketch, "E47.0.15.20", {"center": v(22.07, 43.34) * mm, "radius": 1.5 * mm});
            skCircle(sketch, "E47.0.15.21", {"center": v(12.07, 43.34) * mm, "radius": 1.5 * mm});
            skCircle(sketch, "E47.0.15.22", {"center": v(7.07, 43.34) * mm, "radius": 1.5 * mm});
            skCircle(sketch, "E47.0.15.23", {"center": v(-2.93, 43.34) * mm, "radius": 1.5 * mm});
            skCircle(sketch, "E47.0.16.2", {"center": v(-22.93, 48.34) * mm, "radius": 1.5 * mm});
            skCircle(sketch, "E47.0.16.4", {"center": v(-7.93, 48.34) * mm, "radius": 1.5 * mm});
            skCircle(sketch, "E47.0.16.5", {"center": v(-12.93, 48.34) * mm, "radius": 1.5 * mm});
            skCircle(sketch, "E47.0.16.11", {"center": v(17.07, 48.34) * mm, "radius": 1.5 * mm});
            skCircle(sketch, "E47.0.16.12", {"center": v(2.07, 48.34) * mm, "radius": 1.5 * mm});
            skCircle(sketch, "E47.0.16.15", {"center": v(-17.93, 48.34) * mm, "radius": 1.5 * mm});
            skCircle(sketch, "E47.0.16.20", {"center": v(22.07, 48.34) * mm, "radius": 1.5 * mm});
            skCircle(sketch, "E47.0.16.21", {"center": v(12.07, 48.34) * mm, "radius": 1.5 * mm});
            skCircle(sketch, "E47.0.16.22", {"center": v(7.07, 48.34) * mm, "radius": 1.5 * mm});
            skCircle(sketch, "E47.0.16.23", {"center": v(-2.93, 48.34) * mm, "radius": 1.5 * mm});
            skCircle(sketch, "E47.0.17.2", {"center": v(-22.93, 53.34) * mm, "radius": 1.5 * mm});
            skCircle(sketch, "E47.0.17.4", {"center": v(-7.93, 53.34) * mm, "radius": 1.5 * mm});
            skCircle(sketch, "E47.0.17.5", {"center": v(-12.93, 53.34) * mm, "radius": 1.5 * mm});
            skCircle(sketch, "E47.0.17.11", {"center": v(17.07, 53.34) * mm, "radius": 1.5 * mm});
            skCircle(sketch, "E47.0.17.12", {"center": v(2.07, 53.34) * mm, "radius": 1.5 * mm});
            skCircle(sketch, "E47.0.17.15", {"center": v(-17.93, 53.34) * mm, "radius": 1.5 * mm});
            skCircle(sketch, "E47.0.17.20", {"center": v(22.07, 53.34) * mm, "radius": 1.5 * mm});
            skCircle(sketch, "E47.0.17.21", {"center": v(12.07, 53.34) * mm, "radius": 1.5 * mm});
            skCircle(sketch, "E47.0.17.22", {"center": v(7.07, 53.34) * mm, "radius": 1.5 * mm});
            skCircle(sketch, "E47.0.17.23", {"center": v(-2.93, 53.34) * mm, "radius": 1.5 * mm});
            skCircle(sketch, "E47.0.18.4", {"center": v(-7.93, 58.34) * mm, "radius": 1.5 * mm});
            skCircle(sketch, "E47.0.18.5", {"center": v(-12.93, 58.34) * mm, "radius": 1.5 * mm});
            skCircle(sketch, "E47.0.18.11", {"center": v(17.07, 58.34) * mm, "radius": 1.5 * mm});
            skCircle(sketch, "E47.0.18.12", {"center": v(2.07, 58.34) * mm, "radius": 1.5 * mm});
            skCircle(sketch, "E47.0.18.15", {"center": v(-17.93, 58.34) * mm, "radius": 1.5 * mm});
            skCircle(sketch, "E47.0.18.21", {"center": v(12.07, 58.34) * mm, "radius": 1.5 * mm});
            skCircle(sketch, "E47.0.18.22", {"center": v(7.07, 58.34) * mm, "radius": 1.5 * mm});
            skCircle(sketch, "E47.0.18.23", {"center": v(-2.93, 58.34) * mm, "radius": 1.5 * mm});
            skCircle(sketch, "E47.1.1.1", {"center": v(-32.93, -26.66) * mm, "radius": 1.5 * mm});
            skCircle(sketch, "E47.1.1.2", {"center": v(2.07, -26.66) * mm, "radius": 1.5 * mm});
            skCircle(sketch, "E47.1.1.3", {"center": v(-22.93, -26.66) * mm, "radius": 1.5 * mm});
            skCircle(sketch, "E47.1.1.4", {"center": v(17.07, -26.66) * mm, "radius": 1.5 * mm});
            skCircle(sketch, "E47.1.1.5", {"center": v(12.07, -26.66) * mm, "radius": 1.5 * mm});
            skCircle(sketch, "E47.1.1.6", {"center": v(-12.93, -26.66) * mm, "radius": 1.5 * mm});
            skCircle(sketch, "E47.1.1.11", {"center": v(42.07, -26.66) * mm, "radius": 1.5 * mm});
            skCircle(sketch, "E47.1.1.12", {"center": v(27.07, -26.66) * mm, "radius": 1.5 * mm});
            skCircle(sketch, "E47.1.1.13", {"center": v(-37.93, -26.66) * mm, "radius": 1.5 * mm});
            skCircle(sketch, "E47.1.1.14", {"center": v(-7.93, -26.66) * mm, "radius": 1.5 * mm});
            skCircle(sketch, "E47.1.1.15", {"center": v(7.07, -26.66) * mm, "radius": 1.5 * mm});
            skCircle(sketch, "E47.1.1.16", {"center": v(-2.93, -26.66) * mm, "radius": 1.5 * mm});
            skCircle(sketch, "E47.1.1.20", {"center": v(47.07, -26.66) * mm, "radius": 1.5 * mm});
            skCircle(sketch, "E47.1.1.21", {"center": v(37.07, -26.66) * mm, "radius": 1.5 * mm});
            skCircle(sketch, "E47.1.1.22", {"center": v(32.07, -26.66) * mm, "radius": 1.5 * mm});
            skCircle(sketch, "E47.1.1.23", {"center": v(22.07, -26.66) * mm, "radius": 1.5 * mm});
            skCircle(sketch, "E47.1.1.24", {"center": v(-27.93, -26.66) * mm, "radius": 1.5 * mm});
            skCircle(sketch, "E47.1.1.25", {"center": v(-17.93, -26.66) * mm, "radius": 1.5 * mm});
            skCircle(sketch, "E47.1.2.1", {"center": v(-32.93, -21.66) * mm, "radius": 1.5 * mm});
            skCircle(sketch, "E47.1.2.2", {"center": v(2.07, -21.66) * mm, "radius": 1.5 * mm});
            skCircle(sketch, "E47.1.2.3", {"center": v(-22.93, -21.66) * mm, "radius": 1.5 * mm});
            skCircle(sketch, "E47.1.2.4", {"center": v(17.07, -21.66) * mm, "radius": 1.5 * mm});
            skCircle(sketch, "E47.1.2.5", {"center": v(12.07, -21.66) * mm, "radius": 1.5 * mm});
            skCircle(sketch, "E47.1.2.6", {"center": v(-12.93, -21.66) * mm, "radius": 1.5 * mm});
            skCircle(sketch, "E47.1.2.11", {"center": v(42.07, -21.66) * mm, "radius": 1.5 * mm});
            skCircle(sketch, "E47.1.2.12", {"center": v(27.07, -21.66) * mm, "radius": 1.5 * mm});
            skCircle(sketch, "E47.1.2.13", {"center": v(-37.93, -21.66) * mm, "radius": 1.5 * mm});
            skCircle(sketch, "E47.1.2.14", {"center": v(-7.93, -21.66) * mm, "radius": 1.5 * mm});
            skCircle(sketch, "E47.1.2.15", {"center": v(7.07, -21.66) * mm, "radius": 1.5 * mm});
            skCircle(sketch, "E47.1.2.16", {"center": v(-2.93, -21.66) * mm, "radius": 1.5 * mm});
            skCircle(sketch, "E47.1.2.20", {"center": v(47.07, -21.66) * mm, "radius": 1.5 * mm});
            skCircle(sketch, "E47.1.2.21", {"center": v(37.07, -21.66) * mm, "radius": 1.5 * mm});
            skCircle(sketch, "E47.1.2.22", {"center": v(32.07, -21.66) * mm, "radius": 1.5 * mm});
            skCircle(sketch, "E47.1.2.23", {"center": v(22.07, -21.66) * mm, "radius": 1.5 * mm});
            skCircle(sketch, "E47.1.2.24", {"center": v(-27.93, -21.66) * mm, "radius": 1.5 * mm});
            skCircle(sketch, "E47.1.2.25", {"center": v(-17.93, -21.66) * mm, "radius": 1.5 * mm});
            skCircle(sketch, "E47.1.3.1", {"center": v(-32.93, -16.66) * mm, "radius": 1.5 * mm});
            skCircle(sketch, "E47.1.3.2", {"center": v(2.07, -16.66) * mm, "radius": 1.5 * mm});
            skCircle(sketch, "E47.1.3.3", {"center": v(-22.93, -16.66) * mm, "radius": 1.5 * mm});
            skCircle(sketch, "E47.1.3.4", {"center": v(17.07, -16.66) * mm, "radius": 1.5 * mm});
            skCircle(sketch, "E47.1.3.5", {"center": v(12.07, -16.66) * mm, "radius": 1.5 * mm});
            skCircle(sketch, "E47.1.3.6", {"center": v(-12.93, -16.66) * mm, "radius": 1.5 * mm});
            skCircle(sketch, "E47.1.3.11", {"center": v(42.07, -16.66) * mm, "radius": 1.5 * mm});
            skCircle(sketch, "E47.1.3.12", {"center": v(27.07, -16.66) * mm, "radius": 1.5 * mm});
            skCircle(sketch, "E47.1.3.13", {"center": v(-37.93, -16.66) * mm, "radius": 1.5 * mm});
            skCircle(sketch, "E47.1.3.14", {"center": v(-7.93, -16.66) * mm, "radius": 1.5 * mm});
            skCircle(sketch, "E47.1.3.15", {"center": v(7.07, -16.66) * mm, "radius": 1.5 * mm});
            skCircle(sketch, "E47.1.3.16", {"center": v(-2.93, -16.66) * mm, "radius": 1.5 * mm});
            skCircle(sketch, "E47.1.3.20", {"center": v(47.07, -16.66) * mm, "radius": 1.5 * mm});
            skCircle(sketch, "E47.1.3.21", {"center": v(37.07, -16.66) * mm, "radius": 1.5 * mm});
            skCircle(sketch, "E47.1.3.22", {"center": v(32.07, -16.66) * mm, "radius": 1.5 * mm});
            skCircle(sketch, "E47.1.3.23", {"center": v(22.07, -16.66) * mm, "radius": 1.5 * mm});
            skCircle(sketch, "E47.1.3.24", {"center": v(-27.93, -16.66) * mm, "radius": 1.5 * mm});
            skCircle(sketch, "E47.1.3.25", {"center": v(-17.93, -16.66) * mm, "radius": 1.5 * mm});
            skCircle(sketch, "E47.1.4.1", {"center": v(-32.93, -11.66) * mm, "radius": 1.5 * mm});
            skCircle(sketch, "E47.1.4.2", {"center": v(2.07, -11.66) * mm, "radius": 1.5 * mm});
            skCircle(sketch, "E47.1.4.3", {"center": v(-22.93, -11.66) * mm, "radius": 1.5 * mm});
            skCircle(sketch, "E47.1.4.4", {"center": v(17.07, -11.66) * mm, "radius": 1.5 * mm});
            skCircle(sketch, "E47.1.4.5", {"center": v(12.07, -11.66) * mm, "radius": 1.5 * mm});
            skCircle(sketch, "E47.1.4.6", {"center": v(-12.93, -11.66) * mm, "radius": 1.5 * mm});
            skCircle(sketch, "E47.1.4.11", {"center": v(42.07, -11.66) * mm, "radius": 1.5 * mm});
            skCircle(sketch, "E47.1.4.12", {"center": v(27.07, -11.66) * mm, "radius": 1.5 * mm});
            skCircle(sketch, "E47.1.4.13", {"center": v(-37.93, -11.66) * mm, "radius": 1.5 * mm});
            skCircle(sketch, "E47.1.4.14", {"center": v(-7.93, -11.66) * mm, "radius": 1.5 * mm});
            skCircle(sketch, "E47.1.4.15", {"center": v(7.07, -11.66) * mm, "radius": 1.5 * mm});
            skCircle(sketch, "E47.1.4.16", {"center": v(-2.93, -11.66) * mm, "radius": 1.5 * mm});
            skCircle(sketch, "E47.1.4.20", {"center": v(47.07, -11.66) * mm, "radius": 1.5 * mm});
            skCircle(sketch, "E47.1.4.21", {"center": v(37.07, -11.66) * mm, "radius": 1.5 * mm});
            skCircle(sketch, "E47.1.4.22", {"center": v(32.07, -11.66) * mm, "radius": 1.5 * mm});
            skCircle(sketch, "E47.1.4.23", {"center": v(22.07, -11.66) * mm, "radius": 1.5 * mm});
            skCircle(sketch, "E47.1.4.24", {"center": v(-27.93, -11.66) * mm, "radius": 1.5 * mm});
            skCircle(sketch, "E47.1.4.25", {"center": v(-17.93, -11.66) * mm, "radius": 1.5 * mm});
            skCircle(sketch, "E47.1.5.1", {"center": v(-32.93, -6.66) * mm, "radius": 1.5 * mm});
            skCircle(sketch, "E47.1.5.2", {"center": v(2.07, -6.66) * mm, "radius": 1.5 * mm});
            skCircle(sketch, "E47.1.5.3", {"center": v(-22.93, -6.66) * mm, "radius": 1.5 * mm});
            skCircle(sketch, "E47.1.5.4", {"center": v(17.07, -6.66) * mm, "radius": 1.5 * mm});
            skCircle(sketch, "E47.1.5.5", {"center": v(12.07, -6.66) * mm, "radius": 1.5 * mm});
            skCircle(sketch, "E47.1.5.6", {"center": v(-12.93, -6.66) * mm, "radius": 1.5 * mm});
            skCircle(sketch, "E47.1.5.11", {"center": v(42.07, -6.66) * mm, "radius": 1.5 * mm});
            skCircle(sketch, "E47.1.5.12", {"center": v(27.07, -6.66) * mm, "radius": 1.5 * mm});
            skCircle(sketch, "E47.1.5.13", {"center": v(-37.93, -6.66) * mm, "radius": 1.5 * mm});
            skCircle(sketch, "E47.1.5.14", {"center": v(-7.93, -6.66) * mm, "radius": 1.5 * mm});
            skCircle(sketch, "E47.1.5.15", {"center": v(7.07, -6.66) * mm, "radius": 1.5 * mm});
            skCircle(sketch, "E47.1.5.16", {"center": v(-2.93, -6.66) * mm, "radius": 1.5 * mm});
            skCircle(sketch, "E47.1.5.20", {"center": v(47.07, -6.66) * mm, "radius": 1.5 * mm});
            skCircle(sketch, "E47.1.5.21", {"center": v(37.07, -6.66) * mm, "radius": 1.5 * mm});
            skCircle(sketch, "E47.1.5.22", {"center": v(32.07, -6.66) * mm, "radius": 1.5 * mm});
            skCircle(sketch, "E47.1.5.23", {"center": v(22.07, -6.66) * mm, "radius": 1.5 * mm});
            skCircle(sketch, "E47.1.5.24", {"center": v(-27.93, -6.66) * mm, "radius": 1.5 * mm});
            skCircle(sketch, "E47.1.5.25", {"center": v(-17.93, -6.66) * mm, "radius": 1.5 * mm});
            skCircle(sketch, "E47.1.6.1", {"center": v(-32.93, -1.66) * mm, "radius": 1.5 * mm});
            skCircle(sketch, "E47.1.6.2", {"center": v(2.07, -1.66) * mm, "radius": 1.5 * mm});
            skCircle(sketch, "E47.1.6.3", {"center": v(-22.93, -1.66) * mm, "radius": 1.5 * mm});
            skCircle(sketch, "E47.1.6.4", {"center": v(17.07, -1.66) * mm, "radius": 1.5 * mm});
            skCircle(sketch, "E47.1.6.5", {"center": v(12.07, -1.66) * mm, "radius": 1.5 * mm});
            skCircle(sketch, "E47.1.6.6", {"center": v(-12.93, -1.66) * mm, "radius": 1.5 * mm});
            skCircle(sketch, "E47.1.6.11", {"center": v(42.07, -1.66) * mm, "radius": 1.5 * mm});
            skCircle(sketch, "E47.1.6.12", {"center": v(27.07, -1.66) * mm, "radius": 1.5 * mm});
            skCircle(sketch, "E47.1.6.13", {"center": v(-37.93, -1.66) * mm, "radius": 1.5 * mm});
            skCircle(sketch, "E47.1.6.14", {"center": v(-7.93, -1.66) * mm, "radius": 1.5 * mm});
            skCircle(sketch, "E47.1.6.15", {"center": v(7.07, -1.66) * mm, "radius": 1.5 * mm});
            skCircle(sketch, "E47.1.6.16", {"center": v(-2.93, -1.66) * mm, "radius": 1.5 * mm});
            skCircle(sketch, "E47.1.6.20", {"center": v(47.07, -1.66) * mm, "radius": 1.5 * mm});
            skCircle(sketch, "E47.1.6.21", {"center": v(37.07, -1.66) * mm, "radius": 1.5 * mm});
            skCircle(sketch, "E47.1.6.22", {"center": v(32.07, -1.66) * mm, "radius": 1.5 * mm});
            skCircle(sketch, "E47.1.6.23", {"center": v(22.07, -1.66) * mm, "radius": 1.5 * mm});
            skCircle(sketch, "E47.1.6.24", {"center": v(-27.93, -1.66) * mm, "radius": 1.5 * mm});
            skCircle(sketch, "E47.1.6.25", {"center": v(-17.93, -1.66) * mm, "radius": 1.5 * mm});
            skCircle(sketch, "E47.1.7.1", {"center": v(-32.93, 3.34) * mm, "radius": 1.5 * mm});
            skCircle(sketch, "E47.1.7.2", {"center": v(2.07, 3.34) * mm, "radius": 1.5 * mm});
            skCircle(sketch, "E47.1.7.3", {"center": v(-22.93, 3.34) * mm, "radius": 1.5 * mm});
            skCircle(sketch, "E47.1.7.4", {"center": v(17.07, 3.34) * mm, "radius": 1.5 * mm});
            skCircle(sketch, "E47.1.7.5", {"center": v(12.07, 3.34) * mm, "radius": 1.5 * mm});
            skCircle(sketch, "E47.1.7.6", {"center": v(-12.93, 3.34) * mm, "radius": 1.5 * mm});
            skCircle(sketch, "E47.1.7.11", {"center": v(42.07, 3.34) * mm, "radius": 1.5 * mm});
            skCircle(sketch, "E47.1.7.12", {"center": v(27.07, 3.34) * mm, "radius": 1.5 * mm});
            skCircle(sketch, "E47.1.7.13", {"center": v(-37.93, 3.34) * mm, "radius": 1.5 * mm});
            skCircle(sketch, "E47.1.7.14", {"center": v(-7.93, 3.34) * mm, "radius": 1.5 * mm});
            skCircle(sketch, "E47.1.7.15", {"center": v(7.07, 3.34) * mm, "radius": 1.5 * mm});
            skCircle(sketch, "E47.1.7.16", {"center": v(-2.93, 3.34) * mm, "radius": 1.5 * mm});
            skCircle(sketch, "E47.1.7.20", {"center": v(47.07, 3.34) * mm, "radius": 1.5 * mm});
            skCircle(sketch, "E47.1.7.21", {"center": v(37.07, 3.34) * mm, "radius": 1.5 * mm});
            skCircle(sketch, "E47.1.7.22", {"center": v(32.07, 3.34) * mm, "radius": 1.5 * mm});
            skCircle(sketch, "E47.1.7.23", {"center": v(22.07, 3.34) * mm, "radius": 1.5 * mm});
            skCircle(sketch, "E47.1.7.24", {"center": v(-27.93, 3.34) * mm, "radius": 1.5 * mm});
            skCircle(sketch, "E47.1.7.25", {"center": v(-17.93, 3.34) * mm, "radius": 1.5 * mm});
            skCircle(sketch, "E47.1.8.1", {"center": v(-32.93, 8.34) * mm, "radius": 1.5 * mm});
            skCircle(sketch, "E47.1.8.2", {"center": v(2.07, 8.34) * mm, "radius": 1.5 * mm});
            skCircle(sketch, "E47.1.8.3", {"center": v(-22.93, 8.34) * mm, "radius": 1.5 * mm});
            skCircle(sketch, "E47.1.8.4", {"center": v(17.07, 8.34) * mm, "radius": 1.5 * mm});
            skCircle(sketch, "E47.1.8.5", {"center": v(12.07, 8.34) * mm, "radius": 1.5 * mm});
            skCircle(sketch, "E47.1.8.6", {"center": v(-12.93, 8.34) * mm, "radius": 1.5 * mm});
            skCircle(sketch, "E47.1.8.11", {"center": v(42.07, 8.34) * mm, "radius": 1.5 * mm});
            skCircle(sketch, "E47.1.8.12", {"center": v(27.07, 8.34) * mm, "radius": 1.5 * mm});
            skCircle(sketch, "E47.1.8.13", {"center": v(-37.93, 8.34) * mm, "radius": 1.5 * mm});
            skCircle(sketch, "E47.1.8.14", {"center": v(-7.93, 8.34) * mm, "radius": 1.5 * mm});
            skCircle(sketch, "E47.1.8.15", {"center": v(7.07, 8.34) * mm, "radius": 1.5 * mm});
            skCircle(sketch, "E47.1.8.16", {"center": v(-2.93, 8.34) * mm, "radius": 1.5 * mm});
            skCircle(sketch, "E47.1.8.21", {"center": v(37.07, 8.34) * mm, "radius": 1.5 * mm});
            skCircle(sketch, "E47.1.8.22", {"center": v(32.07, 8.34) * mm, "radius": 1.5 * mm});
            skCircle(sketch, "E47.1.8.23", {"center": v(22.07, 8.34) * mm, "radius": 1.5 * mm});
            skCircle(sketch, "E47.1.8.24", {"center": v(-27.93, 8.34) * mm, "radius": 1.5 * mm});
            skCircle(sketch, "E47.1.8.25", {"center": v(-17.93, 8.34) * mm, "radius": 1.5 * mm});
            skCircle(sketch, "E47.1.9.1", {"center": v(-32.93, 13.34) * mm, "radius": 1.5 * mm});
            skCircle(sketch, "E47.1.9.2", {"center": v(2.07, 13.34) * mm, "radius": 1.5 * mm});
            skCircle(sketch, "E47.1.9.3", {"center": v(-22.93, 13.34) * mm, "radius": 1.5 * mm});
            skCircle(sketch, "E47.1.9.4", {"center": v(17.07, 13.34) * mm, "radius": 1.5 * mm});
            skCircle(sketch, "E47.1.9.5", {"center": v(12.07, 13.34) * mm, "radius": 1.5 * mm});
            skCircle(sketch, "E47.1.9.6", {"center": v(-12.93, 13.34) * mm, "radius": 1.5 * mm});
            skCircle(sketch, "E47.1.9.11", {"center": v(42.07, 13.34) * mm, "radius": 1.5 * mm});
            skCircle(sketch, "E47.1.9.12", {"center": v(27.07, 13.34) * mm, "radius": 1.5 * mm});
            skCircle(sketch, "E47.1.9.13", {"center": v(-37.93, 13.34) * mm, "radius": 1.5 * mm});
            skCircle(sketch, "E47.1.9.14", {"center": v(-7.93, 13.34) * mm, "radius": 1.5 * mm});
            skCircle(sketch, "E47.1.9.15", {"center": v(7.07, 13.34) * mm, "radius": 1.5 * mm});
            skCircle(sketch, "E47.1.9.16", {"center": v(-2.93, 13.34) * mm, "radius": 1.5 * mm});
            skCircle(sketch, "E47.1.9.21", {"center": v(37.07, 13.34) * mm, "radius": 1.5 * mm});
            skCircle(sketch, "E47.1.9.22", {"center": v(32.07, 13.34) * mm, "radius": 1.5 * mm});
            skCircle(sketch, "E47.1.9.23", {"center": v(22.07, 13.34) * mm, "radius": 1.5 * mm});
            skCircle(sketch, "E47.1.9.24", {"center": v(-27.93, 13.34) * mm, "radius": 1.5 * mm});
            skCircle(sketch, "E47.1.9.25", {"center": v(-17.93, 13.34) * mm, "radius": 1.5 * mm});
            skCircle(sketch, "E47.1.10.1", {"center": v(-32.93, 18.34) * mm, "radius": 1.5 * mm});
            skCircle(sketch, "E47.1.10.2", {"center": v(2.07, 18.34) * mm, "radius": 1.5 * mm});
            skCircle(sketch, "E47.1.10.3", {"center": v(-22.93, 18.34) * mm, "radius": 1.5 * mm});
            skCircle(sketch, "E47.1.10.4", {"center": v(17.07, 18.34) * mm, "radius": 1.5 * mm});
            skCircle(sketch, "E47.1.10.5", {"center": v(12.07, 18.34) * mm, "radius": 1.5 * mm});
            skCircle(sketch, "E47.1.10.6", {"center": v(-12.93, 18.34) * mm, "radius": 1.5 * mm});
            skCircle(sketch, "E47.1.10.12", {"center": v(27.07, 18.34) * mm, "radius": 1.5 * mm});
            skCircle(sketch, "E47.1.10.13", {"center": v(-37.93, 18.34) * mm, "radius": 1.5 * mm});
            skCircle(sketch, "E47.1.10.14", {"center": v(-7.93, 18.34) * mm, "radius": 1.5 * mm});
            skCircle(sketch, "E47.1.10.15", {"center": v(7.07, 18.34) * mm, "radius": 1.5 * mm});
            skCircle(sketch, "E47.1.10.16", {"center": v(-2.93, 18.34) * mm, "radius": 1.5 * mm});
            skCircle(sketch, "E47.1.10.21", {"center": v(37.07, 18.34) * mm, "radius": 1.5 * mm});
            skCircle(sketch, "E47.1.10.22", {"center": v(32.07, 18.34) * mm, "radius": 1.5 * mm});
            skCircle(sketch, "E47.1.10.23", {"center": v(22.07, 18.34) * mm, "radius": 1.5 * mm});
            skCircle(sketch, "E47.1.10.24", {"center": v(-27.93, 18.34) * mm, "radius": 1.5 * mm});
            skCircle(sketch, "E47.1.10.25", {"center": v(-17.93, 18.34) * mm, "radius": 1.5 * mm});
            skCircle(sketch, "E47.1.11.1", {"center": v(-32.93, 23.34) * mm, "radius": 1.5 * mm});
            skCircle(sketch, "E47.1.11.2", {"center": v(2.07, 23.34) * mm, "radius": 1.5 * mm});
            skCircle(sketch, "E47.1.11.3", {"center": v(-22.93, 23.34) * mm, "radius": 1.5 * mm});
            skCircle(sketch, "E47.1.11.4", {"center": v(17.07, 23.34) * mm, "radius": 1.5 * mm});
            skCircle(sketch, "E47.1.11.5", {"center": v(12.07, 23.34) * mm, "radius": 1.5 * mm});
            skCircle(sketch, "E47.1.11.6", {"center": v(-12.93, 23.34) * mm, "radius": 1.5 * mm});
            skCircle(sketch, "E47.1.11.12", {"center": v(27.07, 23.34) * mm, "radius": 1.5 * mm});
            skCircle(sketch, "E47.1.11.13", {"center": v(-37.93, 23.34) * mm, "radius": 1.5 * mm});
            skCircle(sketch, "E47.1.11.14", {"center": v(-7.93, 23.34) * mm, "radius": 1.5 * mm});
            skCircle(sketch, "E47.1.11.15", {"center": v(7.07, 23.34) * mm, "radius": 1.5 * mm});
            skCircle(sketch, "E47.1.11.16", {"center": v(-2.93, 23.34) * mm, "radius": 1.5 * mm});
            skCircle(sketch, "E47.1.11.21", {"center": v(37.07, 23.34) * mm, "radius": 1.5 * mm});
            skCircle(sketch, "E47.1.11.22", {"center": v(32.07, 23.34) * mm, "radius": 1.5 * mm});
            skCircle(sketch, "E47.1.11.23", {"center": v(22.07, 23.34) * mm, "radius": 1.5 * mm});
            skCircle(sketch, "E47.1.11.24", {"center": v(-27.93, 23.34) * mm, "radius": 1.5 * mm});
            skCircle(sketch, "E47.1.11.25", {"center": v(-17.93, 23.34) * mm, "radius": 1.5 * mm});
            skCircle(sketch, "E47.1.12.1", {"center": v(-32.93, 28.34) * mm, "radius": 1.5 * mm});
            skCircle(sketch, "E47.1.12.2", {"center": v(2.07, 28.34) * mm, "radius": 1.5 * mm});
            skCircle(sketch, "E47.1.12.3", {"center": v(-22.93, 28.34) * mm, "radius": 1.5 * mm});
            skCircle(sketch, "E47.1.12.4", {"center": v(17.07, 28.34) * mm, "radius": 1.5 * mm});
            skCircle(sketch, "E47.1.12.5", {"center": v(12.07, 28.34) * mm, "radius": 1.5 * mm});
            skCircle(sketch, "E47.1.12.6", {"center": v(-12.93, 28.34) * mm, "radius": 1.5 * mm});
            skCircle(sketch, "E47.1.12.12", {"center": v(27.07, 28.34) * mm, "radius": 1.5 * mm});
            skCircle(sketch, "E47.1.12.14", {"center": v(-7.93, 28.34) * mm, "radius": 1.5 * mm});
            skCircle(sketch, "E47.1.12.15", {"center": v(7.07, 28.34) * mm, "radius": 1.5 * mm});
            skCircle(sketch, "E47.1.12.16", {"center": v(-2.93, 28.34) * mm, "radius": 1.5 * mm});
            skCircle(sketch, "E47.1.12.22", {"center": v(32.07, 28.34) * mm, "radius": 1.5 * mm});
            skCircle(sketch, "E47.1.12.23", {"center": v(22.07, 28.34) * mm, "radius": 1.5 * mm});
            skCircle(sketch, "E47.1.12.24", {"center": v(-27.93, 28.34) * mm, "radius": 1.5 * mm});
            skCircle(sketch, "E47.1.12.25", {"center": v(-17.93, 28.34) * mm, "radius": 1.5 * mm});
            skCircle(sketch, "E47.1.13.1", {"center": v(-32.93, 33.34) * mm, "radius": 1.5 * mm});
            skCircle(sketch, "E47.1.13.2", {"center": v(2.07, 33.34) * mm, "radius": 1.5 * mm});
            skCircle(sketch, "E47.1.13.3", {"center": v(-22.93, 33.34) * mm, "radius": 1.5 * mm});
            skCircle(sketch, "E47.1.13.4", {"center": v(17.07, 33.34) * mm, "radius": 1.5 * mm});
            skCircle(sketch, "E47.1.13.5", {"center": v(12.07, 33.34) * mm, "radius": 1.5 * mm});
            skCircle(sketch, "E47.1.13.6", {"center": v(-12.93, 33.34) * mm, "radius": 1.5 * mm});
            skCircle(sketch, "E47.1.13.12", {"center": v(27.07, 33.34) * mm, "radius": 1.5 * mm});
            skCircle(sketch, "E47.1.13.14", {"center": v(-7.93, 33.34) * mm, "radius": 1.5 * mm});
            skCircle(sketch, "E47.1.13.15", {"center": v(7.07, 33.34) * mm, "radius": 1.5 * mm});
            skCircle(sketch, "E47.1.13.16", {"center": v(-2.93, 33.34) * mm, "radius": 1.5 * mm});
            skCircle(sketch, "E47.1.13.22", {"center": v(32.07, 33.34) * mm, "radius": 1.5 * mm});
            skCircle(sketch, "E47.1.13.23", {"center": v(22.07, 33.34) * mm, "radius": 1.5 * mm});
            skCircle(sketch, "E47.1.13.24", {"center": v(-27.93, 33.34) * mm, "radius": 1.5 * mm});
            skCircle(sketch, "E47.1.13.25", {"center": v(-17.93, 33.34) * mm, "radius": 1.5 * mm});
            skCircle(sketch, "E47.1.14.2", {"center": v(2.07, 38.34) * mm, "radius": 1.5 * mm});
            skCircle(sketch, "E47.1.14.3", {"center": v(-22.93, 38.34) * mm, "radius": 1.5 * mm});
            skCircle(sketch, "E47.1.14.4", {"center": v(17.07, 38.34) * mm, "radius": 1.5 * mm});
            skCircle(sketch, "E47.1.14.5", {"center": v(12.07, 38.34) * mm, "radius": 1.5 * mm});
            skCircle(sketch, "E47.1.14.6", {"center": v(-12.93, 38.34) * mm, "radius": 1.5 * mm});
            skCircle(sketch, "E47.1.14.12", {"center": v(27.07, 38.34) * mm, "radius": 1.5 * mm});
            skCircle(sketch, "E47.1.14.14", {"center": v(-7.93, 38.34) * mm, "radius": 1.5 * mm});
            skCircle(sketch, "E47.1.14.15", {"center": v(7.07, 38.34) * mm, "radius": 1.5 * mm});
            skCircle(sketch, "E47.1.14.16", {"center": v(-2.93, 38.34) * mm, "radius": 1.5 * mm});
            skCircle(sketch, "E47.1.14.22", {"center": v(32.07, 38.34) * mm, "radius": 1.5 * mm});
            skCircle(sketch, "E47.1.14.23", {"center": v(22.07, 38.34) * mm, "radius": 1.5 * mm});
            skCircle(sketch, "E47.1.14.24", {"center": v(-27.93, 38.34) * mm, "radius": 1.5 * mm});
            skCircle(sketch, "E47.1.14.25", {"center": v(-17.93, 38.34) * mm, "radius": 1.5 * mm});
            skCircle(sketch, "E47.1.15.2", {"center": v(2.07, 43.34) * mm, "radius": 1.5 * mm});
            skCircle(sketch, "E47.1.15.3", {"center": v(-22.93, 43.34) * mm, "radius": 1.5 * mm});
            skCircle(sketch, "E47.1.15.4", {"center": v(17.07, 43.34) * mm, "radius": 1.5 * mm});
            skCircle(sketch, "E47.1.15.5", {"center": v(12.07, 43.34) * mm, "radius": 1.5 * mm});
            skCircle(sketch, "E47.1.15.6", {"center": v(-12.93, 43.34) * mm, "radius": 1.5 * mm});
            skCircle(sketch, "E47.1.15.12", {"center": v(27.07, 43.34) * mm, "radius": 1.5 * mm});
            skCircle(sketch, "E47.1.15.14", {"center": v(-7.93, 43.34) * mm, "radius": 1.5 * mm});
            skCircle(sketch, "E47.1.15.15", {"center": v(7.07, 43.34) * mm, "radius": 1.5 * mm});
            skCircle(sketch, "E47.1.15.16", {"center": v(-2.93, 43.34) * mm, "radius": 1.5 * mm});
            skCircle(sketch, "E47.1.15.22", {"center": v(32.07, 43.34) * mm, "radius": 1.5 * mm});
            skCircle(sketch, "E47.1.15.23", {"center": v(22.07, 43.34) * mm, "radius": 1.5 * mm});
            skCircle(sketch, "E47.1.15.24", {"center": v(-27.93, 43.34) * mm, "radius": 1.5 * mm});
            skCircle(sketch, "E47.1.15.25", {"center": v(-17.93, 43.34) * mm, "radius": 1.5 * mm});
            skCircle(sketch, "E47.1.16.2", {"center": v(2.07, 48.34) * mm, "radius": 1.5 * mm});
            skCircle(sketch, "E47.1.16.3", {"center": v(-22.93, 48.34) * mm, "radius": 1.5 * mm});
            skCircle(sketch, "E47.1.16.4", {"center": v(17.07, 48.34) * mm, "radius": 1.5 * mm});
            skCircle(sketch, "E47.1.16.5", {"center": v(12.07, 48.34) * mm, "radius": 1.5 * mm});
            skCircle(sketch, "E47.1.16.6", {"center": v(-12.93, 48.34) * mm, "radius": 1.5 * mm});
            skCircle(sketch, "E47.1.16.14", {"center": v(-7.93, 48.34) * mm, "radius": 1.5 * mm});
            skCircle(sketch, "E47.1.16.15", {"center": v(7.07, 48.34) * mm, "radius": 1.5 * mm});
            skCircle(sketch, "E47.1.16.16", {"center": v(-2.93, 48.34) * mm, "radius": 1.5 * mm});
            skCircle(sketch, "E47.1.16.23", {"center": v(22.07, 48.34) * mm, "radius": 1.5 * mm});
            skCircle(sketch, "E47.1.16.25", {"center": v(-17.93, 48.34) * mm, "radius": 1.5 * mm});
            skCircle(sketch, "E47.1.17.2", {"center": v(2.07, 53.34) * mm, "radius": 1.5 * mm});
            skCircle(sketch, "E47.1.17.3", {"center": v(-22.93, 53.34) * mm, "radius": 1.5 * mm});
            skCircle(sketch, "E47.1.17.4", {"center": v(17.07, 53.34) * mm, "radius": 1.5 * mm});
            skCircle(sketch, "E47.1.17.5", {"center": v(12.07, 53.34) * mm, "radius": 1.5 * mm});
            skCircle(sketch, "E47.1.17.6", {"center": v(-12.93, 53.34) * mm, "radius": 1.5 * mm});
            skCircle(sketch, "E47.1.17.14", {"center": v(-7.93, 53.34) * mm, "radius": 1.5 * mm});
            skCircle(sketch, "E47.1.17.15", {"center": v(7.07, 53.34) * mm, "radius": 1.5 * mm});
            skCircle(sketch, "E47.1.17.16", {"center": v(-2.93, 53.34) * mm, "radius": 1.5 * mm});
            skCircle(sketch, "E47.1.17.23", {"center": v(22.07, 53.34) * mm, "radius": 1.5 * mm});
            skCircle(sketch, "E47.1.17.25", {"center": v(-17.93, 53.34) * mm, "radius": 1.5 * mm});
            skCircle(sketch, "E47.1.18.2", {"center": v(2.07, 58.34) * mm, "radius": 1.5 * mm});
            skCircle(sketch, "E47.1.18.4", {"center": v(17.07, 58.34) * mm, "radius": 1.5 * mm});
            skCircle(sketch, "E47.1.18.5", {"center": v(12.07, 58.34) * mm, "radius": 1.5 * mm});
            skCircle(sketch, "E47.1.18.6", {"center": v(-12.93, 58.34) * mm, "radius": 1.5 * mm});
            skCircle(sketch, "E47.1.18.14", {"center": v(-7.93, 58.34) * mm, "radius": 1.5 * mm});
            skCircle(sketch, "E47.1.18.15", {"center": v(7.07, 58.34) * mm, "radius": 1.5 * mm});
            skCircle(sketch, "E47.1.18.16", {"center": v(-2.93, 58.34) * mm, "radius": 1.5 * mm});
            skCircle(sketch, "E47.1.18.23", {"center": v(22.07, 58.34) * mm, "radius": 1.5 * mm});
            skCircle(sketch, "E47.1.18.25", {"center": v(-17.93, 58.34) * mm, "radius": 1.5 * mm});
            skCircle(sketch, "E47.2.1.1", {"center": v(-7.93, -26.66) * mm, "radius": 1.5 * mm});
            skCircle(sketch, "E47.2.1.2", {"center": v(27.07, -26.66) * mm, "radius": 1.5 * mm});
            skCircle(sketch, "E47.2.1.3", {"center": v(2.07, -26.66) * mm, "radius": 1.5 * mm});
            skCircle(sketch, "E47.2.1.4", {"center": v(42.07, -26.66) * mm, "radius": 1.5 * mm});
            skCircle(sketch, "E47.2.1.5", {"center": v(37.07, -26.66) * mm, "radius": 1.5 * mm});
            skCircle(sketch, "E47.2.1.6", {"center": v(12.07, -26.66) * mm, "radius": 1.5 * mm});
            skCircle(sketch, "E47.2.1.13", {"center": v(-12.93, -26.66) * mm, "radius": 1.5 * mm});
            skCircle(sketch, "E47.2.1.14", {"center": v(17.07, -26.66) * mm, "radius": 1.5 * mm});
            skCircle(sketch, "E47.2.1.15", {"center": v(32.07, -26.66) * mm, "radius": 1.5 * mm});
            skCircle(sketch, "E47.2.1.16", {"center": v(22.07, -26.66) * mm, "radius": 1.5 * mm});
            skCircle(sketch, "E47.2.1.23", {"center": v(47.07, -26.66) * mm, "radius": 1.5 * mm});
            skCircle(sketch, "E47.2.1.24", {"center": v(-2.93, -26.66) * mm, "radius": 1.5 * mm});
            skCircle(sketch, "E47.2.1.25", {"center": v(7.07, -26.66) * mm, "radius": 1.5 * mm});
            skCircle(sketch, "E47.2.2.1", {"center": v(-7.93, -21.66) * mm, "radius": 1.5 * mm});
            skCircle(sketch, "E47.2.2.2", {"center": v(27.07, -21.66) * mm, "radius": 1.5 * mm});
            skCircle(sketch, "E47.2.2.3", {"center": v(2.07, -21.66) * mm, "radius": 1.5 * mm});
            skCircle(sketch, "E47.2.2.4", {"center": v(42.07, -21.66) * mm, "radius": 1.5 * mm});
            skCircle(sketch, "E47.2.2.5", {"center": v(37.07, -21.66) * mm, "radius": 1.5 * mm});
            skCircle(sketch, "E47.2.2.6", {"center": v(12.07, -21.66) * mm, "radius": 1.5 * mm});
            skCircle(sketch, "E47.2.2.13", {"center": v(-12.93, -21.66) * mm, "radius": 1.5 * mm});
            skCircle(sketch, "E47.2.2.14", {"center": v(17.07, -21.66) * mm, "radius": 1.5 * mm});
            skCircle(sketch, "E47.2.2.15", {"center": v(32.07, -21.66) * mm, "radius": 1.5 * mm});
            skCircle(sketch, "E47.2.2.16", {"center": v(22.07, -21.66) * mm, "radius": 1.5 * mm});
            skCircle(sketch, "E47.2.2.23", {"center": v(47.07, -21.66) * mm, "radius": 1.5 * mm});
            skCircle(sketch, "E47.2.2.24", {"center": v(-2.93, -21.66) * mm, "radius": 1.5 * mm});
            skCircle(sketch, "E47.2.2.25", {"center": v(7.07, -21.66) * mm, "radius": 1.5 * mm});
            skCircle(sketch, "E47.2.3.1", {"center": v(-7.93, -16.66) * mm, "radius": 1.5 * mm});
            skCircle(sketch, "E47.2.3.2", {"center": v(27.07, -16.66) * mm, "radius": 1.5 * mm});
            skCircle(sketch, "E47.2.3.3", {"center": v(2.07, -16.66) * mm, "radius": 1.5 * mm});
            skCircle(sketch, "E47.2.3.4", {"center": v(42.07, -16.66) * mm, "radius": 1.5 * mm});
            skCircle(sketch, "E47.2.3.5", {"center": v(37.07, -16.66) * mm, "radius": 1.5 * mm});
            skCircle(sketch, "E47.2.3.6", {"center": v(12.07, -16.66) * mm, "radius": 1.5 * mm});
            skCircle(sketch, "E47.2.3.13", {"center": v(-12.93, -16.66) * mm, "radius": 1.5 * mm});
            skCircle(sketch, "E47.2.3.14", {"center": v(17.07, -16.66) * mm, "radius": 1.5 * mm});
            skCircle(sketch, "E47.2.3.15", {"center": v(32.07, -16.66) * mm, "radius": 1.5 * mm});
            skCircle(sketch, "E47.2.3.16", {"center": v(22.07, -16.66) * mm, "radius": 1.5 * mm});
            skCircle(sketch, "E47.2.3.23", {"center": v(47.07, -16.66) * mm, "radius": 1.5 * mm});
            skCircle(sketch, "E47.2.3.24", {"center": v(-2.93, -16.66) * mm, "radius": 1.5 * mm});
            skCircle(sketch, "E47.2.3.25", {"center": v(7.07, -16.66) * mm, "radius": 1.5 * mm});
            skCircle(sketch, "E47.2.4.1", {"center": v(-7.93, -11.66) * mm, "radius": 1.5 * mm});
            skCircle(sketch, "E47.2.4.2", {"center": v(27.07, -11.66) * mm, "radius": 1.5 * mm});
            skCircle(sketch, "E47.2.4.3", {"center": v(2.07, -11.66) * mm, "radius": 1.5 * mm});
            skCircle(sketch, "E47.2.4.4", {"center": v(42.07, -11.66) * mm, "radius": 1.5 * mm});
            skCircle(sketch, "E47.2.4.5", {"center": v(37.07, -11.66) * mm, "radius": 1.5 * mm});
            skCircle(sketch, "E47.2.4.6", {"center": v(12.07, -11.66) * mm, "radius": 1.5 * mm});
            skCircle(sketch, "E47.2.4.13", {"center": v(-12.93, -11.66) * mm, "radius": 1.5 * mm});
            skCircle(sketch, "E47.2.4.14", {"center": v(17.07, -11.66) * mm, "radius": 1.5 * mm});
            skCircle(sketch, "E47.2.4.15", {"center": v(32.07, -11.66) * mm, "radius": 1.5 * mm});
            skCircle(sketch, "E47.2.4.16", {"center": v(22.07, -11.66) * mm, "radius": 1.5 * mm});
            skCircle(sketch, "E47.2.4.23", {"center": v(47.07, -11.66) * mm, "radius": 1.5 * mm});
            skCircle(sketch, "E47.2.4.24", {"center": v(-2.93, -11.66) * mm, "radius": 1.5 * mm});
            skCircle(sketch, "E47.2.4.25", {"center": v(7.07, -11.66) * mm, "radius": 1.5 * mm});
            skCircle(sketch, "E47.2.5.1", {"center": v(-7.93, -6.66) * mm, "radius": 1.5 * mm});
            skCircle(sketch, "E47.2.5.2", {"center": v(27.07, -6.66) * mm, "radius": 1.5 * mm});
            skCircle(sketch, "E47.2.5.3", {"center": v(2.07, -6.66) * mm, "radius": 1.5 * mm});
            skCircle(sketch, "E47.2.5.4", {"center": v(42.07, -6.66) * mm, "radius": 1.5 * mm});
            skCircle(sketch, "E47.2.5.5", {"center": v(37.07, -6.66) * mm, "radius": 1.5 * mm});
            skCircle(sketch, "E47.2.5.6", {"center": v(12.07, -6.66) * mm, "radius": 1.5 * mm});
            skCircle(sketch, "E47.2.5.13", {"center": v(-12.93, -6.66) * mm, "radius": 1.5 * mm});
            skCircle(sketch, "E47.2.5.14", {"center": v(17.07, -6.66) * mm, "radius": 1.5 * mm});
            skCircle(sketch, "E47.2.5.15", {"center": v(32.07, -6.66) * mm, "radius": 1.5 * mm});
            skCircle(sketch, "E47.2.5.16", {"center": v(22.07, -6.66) * mm, "radius": 1.5 * mm});
            skCircle(sketch, "E47.2.5.23", {"center": v(47.07, -6.66) * mm, "radius": 1.5 * mm});
            skCircle(sketch, "E47.2.5.24", {"center": v(-2.93, -6.66) * mm, "radius": 1.5 * mm});
            skCircle(sketch, "E47.2.5.25", {"center": v(7.07, -6.66) * mm, "radius": 1.5 * mm});
            skCircle(sketch, "E47.2.6.1", {"center": v(-7.93, -1.66) * mm, "radius": 1.5 * mm});
            skCircle(sketch, "E47.2.6.2", {"center": v(27.07, -1.66) * mm, "radius": 1.5 * mm});
            skCircle(sketch, "E47.2.6.3", {"center": v(2.07, -1.66) * mm, "radius": 1.5 * mm});
            skCircle(sketch, "E47.2.6.4", {"center": v(42.07, -1.66) * mm, "radius": 1.5 * mm});
            skCircle(sketch, "E47.2.6.5", {"center": v(37.07, -1.66) * mm, "radius": 1.5 * mm});
            skCircle(sketch, "E47.2.6.6", {"center": v(12.07, -1.66) * mm, "radius": 1.5 * mm});
            skCircle(sketch, "E47.2.6.13", {"center": v(-12.93, -1.66) * mm, "radius": 1.5 * mm});
            skCircle(sketch, "E47.2.6.14", {"center": v(17.07, -1.66) * mm, "radius": 1.5 * mm});
            skCircle(sketch, "E47.2.6.15", {"center": v(32.07, -1.66) * mm, "radius": 1.5 * mm});
            skCircle(sketch, "E47.2.6.16", {"center": v(22.07, -1.66) * mm, "radius": 1.5 * mm});
            skCircle(sketch, "E47.2.6.23", {"center": v(47.07, -1.66) * mm, "radius": 1.5 * mm});
            skCircle(sketch, "E47.2.6.24", {"center": v(-2.93, -1.66) * mm, "radius": 1.5 * mm});
            skCircle(sketch, "E47.2.6.25", {"center": v(7.07, -1.66) * mm, "radius": 1.5 * mm});
            skCircle(sketch, "E47.2.7.1", {"center": v(-7.93, 3.34) * mm, "radius": 1.5 * mm});
            skCircle(sketch, "E47.2.7.2", {"center": v(27.07, 3.34) * mm, "radius": 1.5 * mm});
            skCircle(sketch, "E47.2.7.3", {"center": v(2.07, 3.34) * mm, "radius": 1.5 * mm});
            skCircle(sketch, "E47.2.7.4", {"center": v(42.07, 3.34) * mm, "radius": 1.5 * mm});
            skCircle(sketch, "E47.2.7.5", {"center": v(37.07, 3.34) * mm, "radius": 1.5 * mm});
            skCircle(sketch, "E47.2.7.6", {"center": v(12.07, 3.34) * mm, "radius": 1.5 * mm});
            skCircle(sketch, "E47.2.7.13", {"center": v(-12.93, 3.34) * mm, "radius": 1.5 * mm});
            skCircle(sketch, "E47.2.7.14", {"center": v(17.07, 3.34) * mm, "radius": 1.5 * mm});
            skCircle(sketch, "E47.2.7.15", {"center": v(32.07, 3.34) * mm, "radius": 1.5 * mm});
            skCircle(sketch, "E47.2.7.16", {"center": v(22.07, 3.34) * mm, "radius": 1.5 * mm});
            skCircle(sketch, "E47.2.7.23", {"center": v(47.07, 3.34) * mm, "radius": 1.5 * mm});
            skCircle(sketch, "E47.2.7.24", {"center": v(-2.93, 3.34) * mm, "radius": 1.5 * mm});
            skCircle(sketch, "E47.2.7.25", {"center": v(7.07, 3.34) * mm, "radius": 1.5 * mm});
            skCircle(sketch, "E47.2.8.1", {"center": v(-7.93, 8.34) * mm, "radius": 1.5 * mm});
            skCircle(sketch, "E47.2.8.2", {"center": v(27.07, 8.34) * mm, "radius": 1.5 * mm});
            skCircle(sketch, "E47.2.8.3", {"center": v(2.07, 8.34) * mm, "radius": 1.5 * mm});
            skCircle(sketch, "E47.2.8.4", {"center": v(42.07, 8.34) * mm, "radius": 1.5 * mm});
            skCircle(sketch, "E47.2.8.5", {"center": v(37.07, 8.34) * mm, "radius": 1.5 * mm});
            skCircle(sketch, "E47.2.8.6", {"center": v(12.07, 8.34) * mm, "radius": 1.5 * mm});
            skCircle(sketch, "E47.2.8.13", {"center": v(-12.93, 8.34) * mm, "radius": 1.5 * mm});
            skCircle(sketch, "E47.2.8.14", {"center": v(17.07, 8.34) * mm, "radius": 1.5 * mm});
            skCircle(sketch, "E47.2.8.15", {"center": v(32.07, 8.34) * mm, "radius": 1.5 * mm});
            skCircle(sketch, "E47.2.8.16", {"center": v(22.07, 8.34) * mm, "radius": 1.5 * mm});
            skCircle(sketch, "E47.2.8.24", {"center": v(-2.93, 8.34) * mm, "radius": 1.5 * mm});
            skCircle(sketch, "E47.2.8.25", {"center": v(7.07, 8.34) * mm, "radius": 1.5 * mm});
            skCircle(sketch, "E47.2.9.1", {"center": v(-7.93, 13.34) * mm, "radius": 1.5 * mm});
            skCircle(sketch, "E47.2.9.2", {"center": v(27.07, 13.34) * mm, "radius": 1.5 * mm});
            skCircle(sketch, "E47.2.9.3", {"center": v(2.07, 13.34) * mm, "radius": 1.5 * mm});
            skCircle(sketch, "E47.2.9.4", {"center": v(42.07, 13.34) * mm, "radius": 1.5 * mm});
            skCircle(sketch, "E47.2.9.5", {"center": v(37.07, 13.34) * mm, "radius": 1.5 * mm});
            skCircle(sketch, "E47.2.9.6", {"center": v(12.07, 13.34) * mm, "radius": 1.5 * mm});
            skCircle(sketch, "E47.2.9.13", {"center": v(-12.93, 13.34) * mm, "radius": 1.5 * mm});
            skCircle(sketch, "E47.2.9.14", {"center": v(17.07, 13.34) * mm, "radius": 1.5 * mm});
            skCircle(sketch, "E47.2.9.15", {"center": v(32.07, 13.34) * mm, "radius": 1.5 * mm});
            skCircle(sketch, "E47.2.9.16", {"center": v(22.07, 13.34) * mm, "radius": 1.5 * mm});
            skCircle(sketch, "E47.2.9.24", {"center": v(-2.93, 13.34) * mm, "radius": 1.5 * mm});
            skCircle(sketch, "E47.2.9.25", {"center": v(7.07, 13.34) * mm, "radius": 1.5 * mm});
            skCircle(sketch, "E47.2.10.1", {"center": v(-7.93, 18.34) * mm, "radius": 1.5 * mm});
            skCircle(sketch, "E47.2.10.2", {"center": v(27.07, 18.34) * mm, "radius": 1.5 * mm});
            skCircle(sketch, "E47.2.10.3", {"center": v(2.07, 18.34) * mm, "radius": 1.5 * mm});
            skCircle(sketch, "E47.2.10.5", {"center": v(37.07, 18.34) * mm, "radius": 1.5 * mm});
            skCircle(sketch, "E47.2.10.6", {"center": v(12.07, 18.34) * mm, "radius": 1.5 * mm});
            skCircle(sketch, "E47.2.10.13", {"center": v(-12.93, 18.34) * mm, "radius": 1.5 * mm});
            skCircle(sketch, "E47.2.10.14", {"center": v(17.07, 18.34) * mm, "radius": 1.5 * mm});
            skCircle(sketch, "E47.2.10.15", {"center": v(32.07, 18.34) * mm, "radius": 1.5 * mm});
            skCircle(sketch, "E47.2.10.16", {"center": v(22.07, 18.34) * mm, "radius": 1.5 * mm});
            skCircle(sketch, "E47.2.10.24", {"center": v(-2.93, 18.34) * mm, "radius": 1.5 * mm});
            skCircle(sketch, "E47.2.10.25", {"center": v(7.07, 18.34) * mm, "radius": 1.5 * mm});
            skCircle(sketch, "E47.2.11.1", {"center": v(-7.93, 23.34) * mm, "radius": 1.5 * mm});
            skCircle(sketch, "E47.2.11.2", {"center": v(27.07, 23.34) * mm, "radius": 1.5 * mm});
            skCircle(sketch, "E47.2.11.3", {"center": v(2.07, 23.34) * mm, "radius": 1.5 * mm});
            skCircle(sketch, "E47.2.11.5", {"center": v(37.07, 23.34) * mm, "radius": 1.5 * mm});
            skCircle(sketch, "E47.2.11.6", {"center": v(12.07, 23.34) * mm, "radius": 1.5 * mm});
            skCircle(sketch, "E47.2.11.13", {"center": v(-12.93, 23.34) * mm, "radius": 1.5 * mm});
            skCircle(sketch, "E47.2.11.14", {"center": v(17.07, 23.34) * mm, "radius": 1.5 * mm});
            skCircle(sketch, "E47.2.11.15", {"center": v(32.07, 23.34) * mm, "radius": 1.5 * mm});
            skCircle(sketch, "E47.2.11.16", {"center": v(22.07, 23.34) * mm, "radius": 1.5 * mm});
            skCircle(sketch, "E47.2.11.24", {"center": v(-2.93, 23.34) * mm, "radius": 1.5 * mm});
            skCircle(sketch, "E47.2.11.25", {"center": v(7.07, 23.34) * mm, "radius": 1.5 * mm});
            skCircle(sketch, "E47.2.12.1", {"center": v(-7.93, 28.34) * mm, "radius": 1.5 * mm});
            skCircle(sketch, "E47.2.12.2", {"center": v(27.07, 28.34) * mm, "radius": 1.5 * mm});
            skCircle(sketch, "E47.2.12.3", {"center": v(2.07, 28.34) * mm, "radius": 1.5 * mm});
            skCircle(sketch, "E47.2.12.5", {"center": v(37.07, 28.34) * mm, "radius": 1.5 * mm});
            skCircle(sketch, "E47.2.12.6", {"center": v(12.07, 28.34) * mm, "radius": 1.5 * mm});
            skCircle(sketch, "E47.2.12.13", {"center": v(-12.93, 28.34) * mm, "radius": 1.5 * mm});
            skCircle(sketch, "E47.2.12.14", {"center": v(17.07, 28.34) * mm, "radius": 1.5 * mm});
            skCircle(sketch, "E47.2.12.15", {"center": v(32.07, 28.34) * mm, "radius": 1.5 * mm});
            skCircle(sketch, "E47.2.12.16", {"center": v(22.07, 28.34) * mm, "radius": 1.5 * mm});
            skCircle(sketch, "E47.2.12.24", {"center": v(-2.93, 28.34) * mm, "radius": 1.5 * mm});
            skCircle(sketch, "E47.2.12.25", {"center": v(7.07, 28.34) * mm, "radius": 1.5 * mm});
            skCircle(sketch, "E47.2.13.1", {"center": v(-7.93, 33.34) * mm, "radius": 1.5 * mm});
            skCircle(sketch, "E47.2.13.2", {"center": v(27.07, 33.34) * mm, "radius": 1.5 * mm});
            skCircle(sketch, "E47.2.13.3", {"center": v(2.07, 33.34) * mm, "radius": 1.5 * mm});
            skCircle(sketch, "E47.2.13.6", {"center": v(12.07, 33.34) * mm, "radius": 1.5 * mm});
            skCircle(sketch, "E47.2.13.13", {"center": v(-12.93, 33.34) * mm, "radius": 1.5 * mm});
            skCircle(sketch, "E47.2.13.14", {"center": v(17.07, 33.34) * mm, "radius": 1.5 * mm});
            skCircle(sketch, "E47.2.13.15", {"center": v(32.07, 33.34) * mm, "radius": 1.5 * mm});
            skCircle(sketch, "E47.2.13.16", {"center": v(22.07, 33.34) * mm, "radius": 1.5 * mm});
            skCircle(sketch, "E47.2.13.24", {"center": v(-2.93, 33.34) * mm, "radius": 1.5 * mm});
            skCircle(sketch, "E47.2.13.25", {"center": v(7.07, 33.34) * mm, "radius": 1.5 * mm});
            skCircle(sketch, "E47.2.14.1", {"center": v(-7.93, 38.34) * mm, "radius": 1.5 * mm});
            skCircle(sketch, "E47.2.14.2", {"center": v(27.07, 38.34) * mm, "radius": 1.5 * mm});
            skCircle(sketch, "E47.2.14.3", {"center": v(2.07, 38.34) * mm, "radius": 1.5 * mm});
            skCircle(sketch, "E47.2.14.6", {"center": v(12.07, 38.34) * mm, "radius": 1.5 * mm});
            skCircle(sketch, "E47.2.14.13", {"center": v(-12.93, 38.34) * mm, "radius": 1.5 * mm});
            skCircle(sketch, "E47.2.14.14", {"center": v(17.07, 38.34) * mm, "radius": 1.5 * mm});
            skCircle(sketch, "E47.2.14.15", {"center": v(32.07, 38.34) * mm, "radius": 1.5 * mm});
            skCircle(sketch, "E47.2.14.24", {"center": v(-2.93, 38.34) * mm, "radius": 1.5 * mm});
            skCircle(sketch, "E47.2.14.25", {"center": v(7.07, 38.34) * mm, "radius": 1.5 * mm});
            skCircle(sketch, "E47.2.15.1", {"center": v(-7.93, 43.34) * mm, "radius": 1.5 * mm});
            skCircle(sketch, "E47.2.15.2", {"center": v(27.07, 43.34) * mm, "radius": 1.5 * mm});
            skCircle(sketch, "E47.2.15.3", {"center": v(2.07, 43.34) * mm, "radius": 1.5 * mm});
            skCircle(sketch, "E47.2.15.6", {"center": v(12.07, 43.34) * mm, "radius": 1.5 * mm});
            skCircle(sketch, "E47.2.15.13", {"center": v(-12.93, 43.34) * mm, "radius": 1.5 * mm});
            skCircle(sketch, "E47.2.15.14", {"center": v(17.07, 43.34) * mm, "radius": 1.5 * mm});
            skCircle(sketch, "E47.2.15.15", {"center": v(32.07, 43.34) * mm, "radius": 1.5 * mm});
            skCircle(sketch, "E47.2.15.16", {"center": v(22.07, 43.34) * mm, "radius": 1.5 * mm});
            skCircle(sketch, "E47.2.15.24", {"center": v(-2.93, 43.34) * mm, "radius": 1.5 * mm});
            skCircle(sketch, "E47.2.15.25", {"center": v(7.07, 43.34) * mm, "radius": 1.5 * mm});
            skCircle(sketch, "E47.2.16.1", {"center": v(-7.93, 48.34) * mm, "radius": 1.5 * mm});
            skCircle(sketch, "E47.2.16.3", {"center": v(2.07, 48.34) * mm, "radius": 1.5 * mm});
            skCircle(sketch, "E47.2.16.6", {"center": v(12.07, 48.34) * mm, "radius": 1.5 * mm});
            skCircle(sketch, "E47.2.16.13", {"center": v(-12.93, 48.34) * mm, "radius": 1.5 * mm});
            skCircle(sketch, "E47.2.16.14", {"center": v(17.07, 48.34) * mm, "radius": 1.5 * mm});
            skCircle(sketch, "E47.2.16.16", {"center": v(22.07, 48.34) * mm, "radius": 1.5 * mm});
            skCircle(sketch, "E47.2.16.24", {"center": v(-2.93, 48.34) * mm, "radius": 1.5 * mm});
            skCircle(sketch, "E47.2.16.25", {"center": v(7.07, 48.34) * mm, "radius": 1.5 * mm});
            skCircle(sketch, "E47.2.17.1", {"center": v(-7.93, 53.34) * mm, "radius": 1.5 * mm});
            skCircle(sketch, "E47.2.17.3", {"center": v(2.07, 53.34) * mm, "radius": 1.5 * mm});
            skCircle(sketch, "E47.2.17.6", {"center": v(12.07, 53.34) * mm, "radius": 1.5 * mm});
            skCircle(sketch, "E47.2.17.13", {"center": v(-12.93, 53.34) * mm, "radius": 1.5 * mm});
            skCircle(sketch, "E47.2.17.14", {"center": v(17.07, 53.34) * mm, "radius": 1.5 * mm});
            skCircle(sketch, "E47.2.17.16", {"center": v(22.07, 53.34) * mm, "radius": 1.5 * mm});
            skCircle(sketch, "E47.2.17.24", {"center": v(-2.93, 53.34) * mm, "radius": 1.5 * mm});
            skCircle(sketch, "E47.2.17.25", {"center": v(7.07, 53.34) * mm, "radius": 1.5 * mm});
            skCircle(sketch, "E47.2.18.1", {"center": v(-7.93, 58.34) * mm, "radius": 1.5 * mm});
            skCircle(sketch, "E47.2.18.3", {"center": v(2.07, 58.34) * mm, "radius": 1.5 * mm});
            skCircle(sketch, "E47.2.18.6", {"center": v(12.07, 58.34) * mm, "radius": 1.5 * mm});
            skCircle(sketch, "E47.2.18.13", {"center": v(-12.93, 58.34) * mm, "radius": 1.5 * mm});
            skCircle(sketch, "E47.2.18.14", {"center": v(17.07, 58.34) * mm, "radius": 1.5 * mm});
            skCircle(sketch, "E47.2.18.16", {"center": v(22.07, 58.34) * mm, "radius": 1.5 * mm});
            skCircle(sketch, "E47.2.18.24", {"center": v(-2.93, 58.34) * mm, "radius": 1.5 * mm});
            skCircle(sketch, "E47.2.18.25", {"center": v(7.07, 58.34) * mm, "radius": 1.5 * mm});
            skCircle(sketch, "E48.0.16.2", {"center": v(-17.93, 64.1) * mm, "radius": 1.5 * mm});
            skCircle(sketch, "E48.0.16.4", {"center": v(-2.93, 64.1) * mm, "radius": 1.5 * mm});
            skCircle(sketch, "E48.0.16.5", {"center": v(-7.93, 64.1) * mm, "radius": 1.5 * mm});
            skCircle(sketch, "E48.0.16.11", {"center": v(22.07, 64.1) * mm, "radius": 1.5 * mm});
            skCircle(sketch, "E48.0.16.12", {"center": v(7.07, 64.1) * mm, "radius": 1.5 * mm});
            skCircle(sketch, "E48.0.16.15", {"center": v(-12.93, 64.1) * mm, "radius": 1.5 * mm});
            skCircle(sketch, "E48.0.16.21", {"center": v(17.07, 64.1) * mm, "radius": 1.5 * mm});
            skCircle(sketch, "E48.0.16.22", {"center": v(12.07, 64.1) * mm, "radius": 1.5 * mm});
            skCircle(sketch, "E48.0.16.23", {"center": v(2.07, 64.1) * mm, "radius": 1.5 * mm});
            skCircle(sketch, "E48.0.17.2", {"center": v(-17.93, 69.1) * mm, "radius": 1.5 * mm});
            skCircle(sketch, "E48.0.17.4", {"center": v(-2.93, 69.1) * mm, "radius": 1.5 * mm});
            skCircle(sketch, "E48.0.17.5", {"center": v(-7.93, 69.1) * mm, "radius": 1.5 * mm});
            skCircle(sketch, "E48.0.17.11", {"center": v(22.07, 69.1) * mm, "radius": 1.5 * mm});
            skCircle(sketch, "E48.0.17.12", {"center": v(7.07, 69.1) * mm, "radius": 1.5 * mm});
            skCircle(sketch, "E48.0.17.15", {"center": v(-12.93, 69.1) * mm, "radius": 1.5 * mm});
            skCircle(sketch, "E48.0.17.21", {"center": v(17.07, 69.1) * mm, "radius": 1.5 * mm});
            skCircle(sketch, "E48.0.17.22", {"center": v(12.07, 69.1) * mm, "radius": 1.5 * mm});
            skCircle(sketch, "E48.0.17.23", {"center": v(2.07, 69.1) * mm, "radius": 1.5 * mm});
            skCircle(sketch, "E48.0.18.4", {"center": v(-2.93, 74.1) * mm, "radius": 1.5 * mm});
            skCircle(sketch, "E48.0.18.5", {"center": v(-7.93, 74.1) * mm, "radius": 1.5 * mm});
            skCircle(sketch, "E48.0.18.12", {"center": v(7.07, 74.1) * mm, "radius": 1.5 * mm});
            skCircle(sketch, "E48.0.18.15", {"center": v(-12.93, 74.1) * mm, "radius": 1.5 * mm});
            skCircle(sketch, "E48.0.18.21", {"center": v(17.07, 74.1) * mm, "radius": 1.5 * mm});
            skCircle(sketch, "E48.0.18.22", {"center": v(12.07, 74.1) * mm, "radius": 1.5 * mm});
            skCircle(sketch, "E48.0.18.23", {"center": v(2.07, 74.1) * mm, "radius": 1.5 * mm});
            skCircle(sketch, "E48.1.16.2", {"center": v(7.07, 64.1) * mm, "radius": 1.5 * mm});
            skCircle(sketch, "E48.1.16.3", {"center": v(-17.93, 64.1) * mm, "radius": 1.5 * mm});
            skCircle(sketch, "E48.1.16.4", {"center": v(22.07, 64.1) * mm, "radius": 1.5 * mm});
            skCircle(sketch, "E48.1.16.5", {"center": v(17.07, 64.1) * mm, "radius": 1.5 * mm});
            skCircle(sketch, "E48.1.16.6", {"center": v(-7.93, 64.1) * mm, "radius": 1.5 * mm});
            skCircle(sketch, "E48.1.16.14", {"center": v(-2.93, 64.1) * mm, "radius": 1.5 * mm});
            skCircle(sketch, "E48.1.16.15", {"center": v(12.07, 64.1) * mm, "radius": 1.5 * mm});
            skCircle(sketch, "E48.1.16.16", {"center": v(2.07, 64.1) * mm, "radius": 1.5 * mm});
            skCircle(sketch, "E48.1.17.2", {"center": v(7.07, 69.1) * mm, "radius": 1.5 * mm});
            skCircle(sketch, "E48.1.17.3", {"center": v(-17.93, 69.1) * mm, "radius": 1.5 * mm});
            skCircle(sketch, "E48.1.17.4", {"center": v(22.07, 69.1) * mm, "radius": 1.5 * mm});
            skCircle(sketch, "E48.1.17.5", {"center": v(17.07, 69.1) * mm, "radius": 1.5 * mm});
            skCircle(sketch, "E48.1.17.6", {"center": v(-7.93, 69.1) * mm, "radius": 1.5 * mm});
            skCircle(sketch, "E48.1.17.14", {"center": v(-2.93, 69.1) * mm, "radius": 1.5 * mm});
            skCircle(sketch, "E48.1.17.15", {"center": v(12.07, 69.1) * mm, "radius": 1.5 * mm});
            skCircle(sketch, "E48.1.17.16", {"center": v(2.07, 69.1) * mm, "radius": 1.5 * mm});
            skCircle(sketch, "E48.1.17.25", {"center": v(-12.93, 69.1) * mm, "radius": 1.5 * mm});
            skCircle(sketch, "E48.1.18.2", {"center": v(7.07, 74.1) * mm, "radius": 1.5 * mm});
            skCircle(sketch, "E48.1.18.5", {"center": v(17.07, 74.1) * mm, "radius": 1.5 * mm});
            skCircle(sketch, "E48.1.18.6", {"center": v(-7.93, 74.1) * mm, "radius": 1.5 * mm});
            skCircle(sketch, "E48.1.18.14", {"center": v(-2.93, 74.1) * mm, "radius": 1.5 * mm});
            skCircle(sketch, "E48.1.18.15", {"center": v(12.07, 74.1) * mm, "radius": 1.5 * mm});
            skCircle(sketch, "E48.1.18.16", {"center": v(2.07, 74.1) * mm, "radius": 1.5 * mm});
            skCircle(sketch, "E48.1.18.25", {"center": v(-12.93, 74.1) * mm, "radius": 1.5 * mm});
            skCircle(sketch, "E48.2.16.1", {"center": v(-2.93, 64.1) * mm, "radius": 1.5 * mm});
            skCircle(sketch, "E48.2.16.3", {"center": v(7.07, 64.1) * mm, "radius": 1.5 * mm});
            skCircle(sketch, "E48.2.16.6", {"center": v(17.07, 64.1) * mm, "radius": 1.5 * mm});
            skCircle(sketch, "E48.2.16.13", {"center": v(-7.93, 64.1) * mm, "radius": 1.5 * mm});
            skCircle(sketch, "E48.2.16.14", {"center": v(22.07, 64.1) * mm, "radius": 1.5 * mm});
            skCircle(sketch, "E48.2.16.24", {"center": v(2.07, 64.1) * mm, "radius": 1.5 * mm});
            skCircle(sketch, "E48.2.16.25", {"center": v(12.07, 64.1) * mm, "radius": 1.5 * mm});
            skCircle(sketch, "E48.2.17.1", {"center": v(-2.93, 69.1) * mm, "radius": 1.5 * mm});
            skCircle(sketch, "E48.2.17.3", {"center": v(7.07, 69.1) * mm, "radius": 1.5 * mm});
            skCircle(sketch, "E48.2.17.6", {"center": v(17.07, 69.1) * mm, "radius": 1.5 * mm});
            skCircle(sketch, "E48.2.17.13", {"center": v(-7.93, 69.1) * mm, "radius": 1.5 * mm});
            skCircle(sketch, "E48.2.17.14", {"center": v(22.07, 69.1) * mm, "radius": 1.5 * mm});
            skCircle(sketch, "E48.2.17.24", {"center": v(2.07, 69.1) * mm, "radius": 1.5 * mm});
            skCircle(sketch, "E48.2.17.25", {"center": v(12.07, 69.1) * mm, "radius": 1.5 * mm});
            skCircle(sketch, "E48.2.18.1", {"center": v(-2.93, 74.1) * mm, "radius": 1.5 * mm});
            skCircle(sketch, "E48.2.18.3", {"center": v(7.07, 74.1) * mm, "radius": 1.5 * mm});
            skCircle(sketch, "E48.2.18.6", {"center": v(17.07, 74.1) * mm, "radius": 1.5 * mm});
            skCircle(sketch, "E48.2.18.13", {"center": v(-7.93, 74.1) * mm, "radius": 1.5 * mm});
            skCircle(sketch, "E48.2.18.25", {"center": v(12.07, 74.1) * mm, "radius": 1.5 * mm});
            skSolve(sketch);
        }
        {
            var Q0;
            Q0=qSketchRegion(id+"F14",true);
            extrude(context, id + "F15", {"entities" : qUnion([Q0]), "operationType" : NewBodyOperationType.REMOVE, "endBound" : BoundingType.UP_TO_NEXT, "oppositeDirection" : true, "depth" : 25 * mm, "offsetDistance" : 25 * mm});
        }
    });
